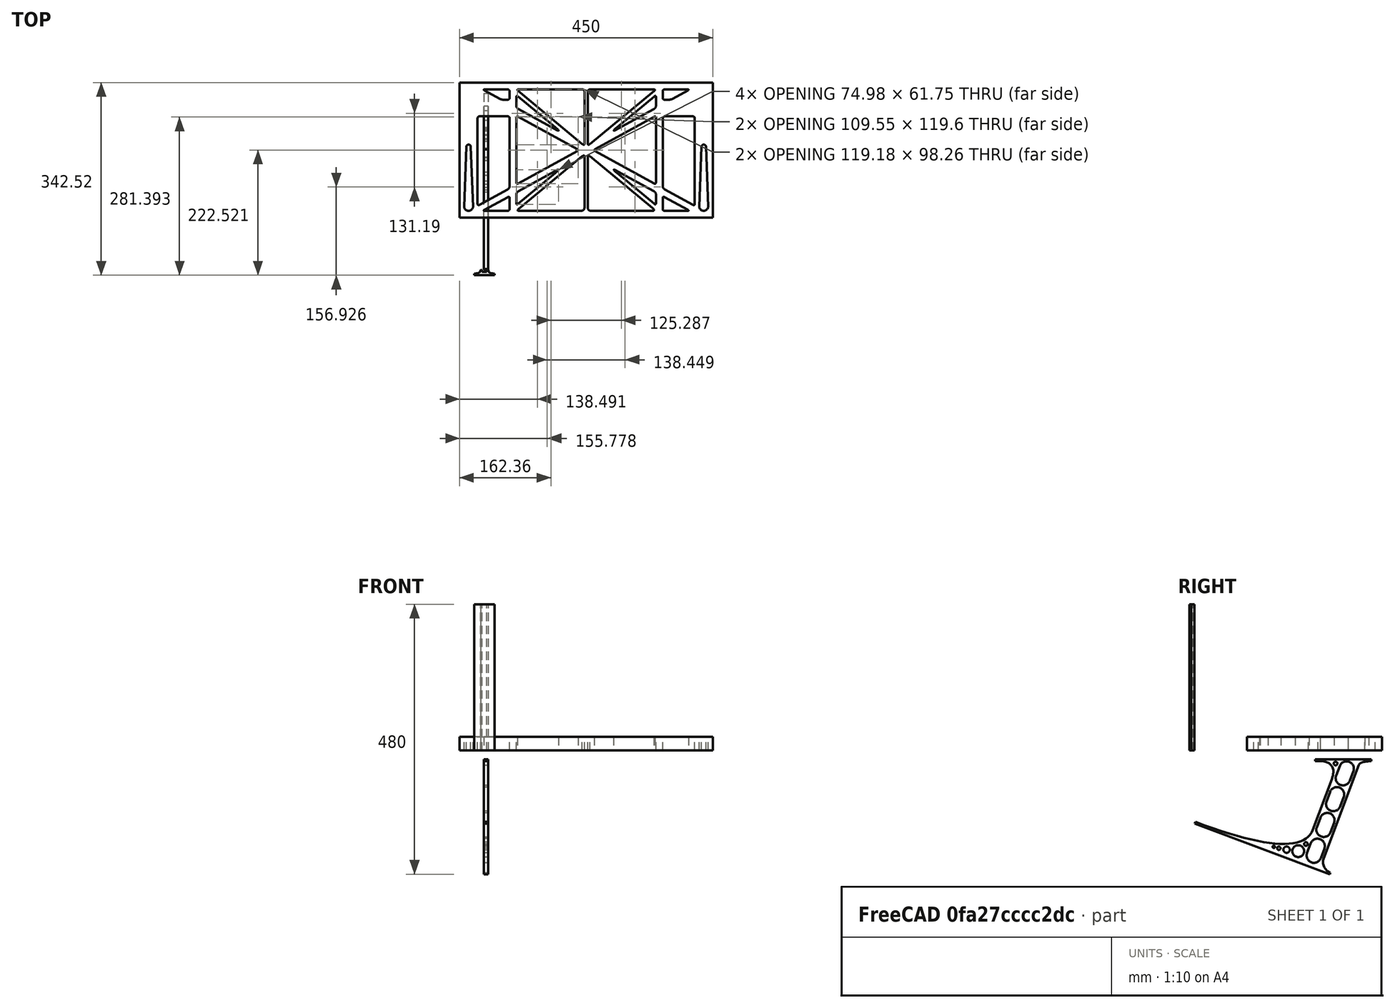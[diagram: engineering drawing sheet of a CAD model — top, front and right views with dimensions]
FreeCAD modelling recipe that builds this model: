
FCSTD DOCUMENT  (FreeCAD 0.19R0.19.2)
Label: laptopStand167FCStd
License: All rights reserved
LicenseURL: http://en.wikipedia.org/wiki/All_rights_reserved
objects: Sketcher::SketchObject×4, Part::Extrusion×3
note: 7 computed .brp shape members not serialized (recipe doc carries the construction recipe); baked Part::Feature solids carry a one-line shape summary decoded from their .brp

FEATURE [Sketcher::SketchObject] Sketch
  FullyConstrained = false
  sketch-geometry (349):
    g0: LineSegment StartX=-10.9272 StartY=-82.7794 StartZ=0 EndX=46.0728 EndY=-51.4823 EndZ=0
    g1: LineSegment StartX=-10.9272 StartY=76.4095 StartZ=0 EndX=-10.9272 EndY=-82.7794 EndZ=0
    g2: LineSegment StartX=46.0728 StartY=76.4095 StartZ=0 EndX=46.0728 EndY=-51.4823 EndZ=0
    g3: LineSegment StartX=-42.9272 StartY=136.221 StartZ=0 EndX=-42.9272 EndY=-103.779 EndZ=0
    g4: LineSegment StartX=407.073 StartY=136.221 StartZ=0 EndX=407.073 EndY=-103.779 EndZ=0
    g5: ArcOfCircle CenterX=-26.9272 CenterY=-83.7794 CenterZ=0 NormalX=0 NormalY=0 NormalZ=1 AngleXU=0 Radius=8 StartAngle=3.14159 EndAngle=6.28319
    g6: ArcOfCircle CenterX=391.073 CenterY=22.1087 CenterZ=0 NormalX=0 NormalY=0 NormalZ=1 AngleXU=0 Radius=8 StartAngle=-4.4e-15 EndAngle=3.14159
    g7: LineSegment StartX=399.073 StartY=22.1087 StartZ=0 EndX=399.073 EndY=-83.7794 EndZ=0
    g8: LineSegment StartX=383.073 StartY=22.1087 StartZ=0 EndX=383.073 EndY=-83.7794 EndZ=0
    g9: ArcOfCircle CenterX=391.073 CenterY=-83.7794 CenterZ=0 NormalX=0 NormalY=0 NormalZ=1 AngleXU=0 Radius=8 StartAngle=3.14159 EndAngle=6.28319
    g10: Circle CenterX=175.022 CenterY=27.0628 CenterZ=0 NormalX=0 NormalY=0 NormalZ=1 AngleXU=0 Radius=1
    g11: Circle CenterX=179.022 CenterY=24.8665 CenterZ=0 NormalX=0 NormalY=0 NormalZ=1 AngleXU=0 Radius=1
    g12: Circle CenterX=179.022 CenterY=27.0628 CenterZ=0 NormalX=0 NormalY=0 NormalZ=1 AngleXU=0 Radius=1
    g13: BSplineCurve PolesCount=3 KnotsCount=2 Degree=2 IsPeriodic=0
    g14: GeomPoint X=175.022 Y=27.0628 Z=0
    g15: GeomPoint X=179.022 Y=27.0628 Z=0
    g16: Circle CenterX=189.124 CenterY=27.0628 CenterZ=0 NormalX=0 NormalY=0 NormalZ=1 AngleXU=0 Radius=1
    g17: Circle CenterX=185.124 CenterY=24.8665 CenterZ=0 NormalX=0 NormalY=0 NormalZ=1 AngleXU=0 Radius=1
    g18: Circle CenterX=185.124 CenterY=27.0628 CenterZ=0 NormalX=0 NormalY=0 NormalZ=1 AngleXU=0 Radius=1
    g19: BSplineCurve PolesCount=3 KnotsCount=2 Degree=2 IsPeriodic=0
    g20: GeomPoint X=189.124 Y=27.0628 Z=0
    g21: GeomPoint X=185.124 Y=27.0628 Z=0
    g22: Circle CenterX=175.022 CenterY=5.37834 CenterZ=0 NormalX=0 NormalY=0 NormalZ=1 AngleXU=0 Radius=1
    g23: Circle CenterX=179.022 CenterY=7.57463 CenterZ=0 NormalX=0 NormalY=0 NormalZ=1 AngleXU=0 Radius=1
    g24: Circle CenterX=179.022 CenterY=5.34704 CenterZ=0 NormalX=0 NormalY=0 NormalZ=1 AngleXU=0 Radius=1
    g25: BSplineCurve PolesCount=3 KnotsCount=2 Degree=2 IsPeriodic=0
    g26: GeomPoint X=175.022 Y=5.37834 Z=0
    g27: GeomPoint X=179.022 Y=5.34704 Z=0
    g28: Circle CenterX=189.124 CenterY=5.37834 CenterZ=0 NormalX=0 NormalY=0 NormalZ=1 AngleXU=0 Radius=1
    g29: Circle CenterX=185.124 CenterY=7.57463 CenterZ=0 NormalX=0 NormalY=0 NormalZ=1 AngleXU=0 Radius=1
    g30: Circle CenterX=185.124 CenterY=5.34704 CenterZ=0 NormalX=0 NormalY=0 NormalZ=1 AngleXU=0 Radius=1
    g31: BSplineCurve PolesCount=3 KnotsCount=2 Degree=2 IsPeriodic=0
    g32: GeomPoint X=189.124 Y=5.37834 Z=0
    g33: GeomPoint X=185.124 Y=5.34704 Z=0
    g34: Circle CenterX=165.871 CenterY=18.1458 CenterZ=0 NormalX=0 NormalY=0 NormalZ=1 AngleXU=0 Radius=1
    g35: Circle CenterX=169.377 CenterY=16.2206 CenterZ=0 NormalX=0 NormalY=0 NormalZ=1 AngleXU=0 Radius=1
    g36: Circle CenterX=165.871 CenterY=14.2954 CenterZ=0 NormalX=0 NormalY=0 NormalZ=1 AngleXU=0 Radius=1
    g37: BSplineCurve PolesCount=3 KnotsCount=2 Degree=2 IsPeriodic=0
    g38: GeomPoint X=165.871 Y=18.1458 Z=0
    g39: GeomPoint X=165.871 Y=14.2954 Z=0
    g40: Circle CenterX=198.275 CenterY=18.1458 CenterZ=0 NormalX=0 NormalY=0 NormalZ=1 AngleXU=0 Radius=1
    g41: Circle CenterX=194.768 CenterY=16.2206 CenterZ=0 NormalX=0 NormalY=0 NormalZ=1 AngleXU=0 Radius=1
    g42: Circle CenterX=198.275 CenterY=14.2954 CenterZ=0 NormalX=0 NormalY=0 NormalZ=1 AngleXU=0 Radius=1
    g43: BSplineCurve PolesCount=3 KnotsCount=2 Degree=2 IsPeriodic=0
    g44: GeomPoint X=198.275 Y=18.1458 Z=0
    g45: GeomPoint X=198.275 Y=14.2954 Z=0
    g46: LineSegment StartX=407.073 StartY=-103.779 StartZ=0 EndX=-42.9272 EndY=-103.779 EndZ=0
    g47: LineSegment StartX=407.073 StartY=136.221 StartZ=0 EndX=-42.9272 EndY=136.221 EndZ=0
    g48: LineSegment StartX=46.0728 StartY=76.4095 StartZ=0 EndX=-10.9272 EndY=76.4095 EndZ=0
    g49: Circle CenterX=125.607 CenterY=54.1951 CenterZ=0 NormalX=0 NormalY=0 NormalZ=1 AngleXU=0 Radius=1
    g50: Circle CenterX=139.632 CenterY=46.4944 CenterZ=0 NormalX=0 NormalY=0 NormalZ=1 AngleXU=0 Radius=1
    g51: Circle CenterX=127.326 CenterY=56.7187 CenterZ=0 NormalX=0 NormalY=0 NormalZ=1 AngleXU=0 Radius=1
    g52: BSplineCurve PolesCount=3 KnotsCount=2 Degree=2 IsPeriodic=0
    g53: GeomPoint X=125.607 Y=54.1951 Z=0
    g54: GeomPoint X=127.326 Y=56.7187 Z=0
    g55: Circle CenterX=236.821 CenterY=56.7187 CenterZ=0 NormalX=0 NormalY=0 NormalZ=1 AngleXU=0 Radius=1
    g56: Circle CenterX=224.513 CenterY=46.4944 CenterZ=0 NormalX=0 NormalY=0 NormalZ=1 AngleXU=0 Radius=1
    g57: Circle CenterX=238.538 CenterY=54.1951 CenterZ=0 NormalX=0 NormalY=0 NormalZ=1 AngleXU=0 Radius=1
    g58: BSplineCurve PolesCount=3 KnotsCount=2 Degree=2 IsPeriodic=0
    g59: GeomPoint X=236.821 Y=56.7187 Z=0
    g60: GeomPoint X=238.538 Y=54.1951 Z=0
    g61: Circle CenterX=238.538 CenterY=-21.7539 CenterZ=0 NormalX=0 NormalY=0 NormalZ=1 AngleXU=0 Radius=1
    g62: Circle CenterX=224.513 CenterY=-14.0532 CenterZ=0 NormalX=0 NormalY=0 NormalZ=1 AngleXU=0 Radius=1
    g63: Circle CenterX=236.821 CenterY=-24.2775 CenterZ=0 NormalX=0 NormalY=0 NormalZ=1 AngleXU=0 Radius=1
    g64: BSplineCurve PolesCount=3 KnotsCount=2 Degree=2 IsPeriodic=0
    g65: GeomPoint X=238.538 Y=-21.7539 Z=0
    g66: GeomPoint X=236.821 Y=-24.2775 Z=0
    g67: Circle CenterX=125.607 CenterY=-21.7539 CenterZ=0 NormalX=0 NormalY=0 NormalZ=1 AngleXU=0 Radius=1
    g68: Circle CenterX=139.632 CenterY=-14.0532 CenterZ=0 NormalX=0 NormalY=0 NormalZ=1 AngleXU=0 Radius=1
    g69: Circle CenterX=127.325 CenterY=-24.2775 CenterZ=0 NormalX=0 NormalY=0 NormalZ=1 AngleXU=0 Radius=1
    g70: BSplineCurve PolesCount=3 KnotsCount=2 Degree=2 IsPeriodic=0
    g71: GeomPoint X=125.607 Y=-21.7539 Z=0
    g72: GeomPoint X=127.325 Y=-24.2775 Z=0
    g73: Circle CenterX=302.996 CenterY=111.695 CenterZ=0 NormalX=0 NormalY=0 NormalZ=1 AngleXU=0 Radius=1
    g74: Circle CenterX=306.073 CenterY=114.251 CenterZ=0 NormalX=0 NormalY=0 NormalZ=1 AngleXU=0 Radius=1
    g75: Circle CenterX=306.073 CenterY=110.251 CenterZ=0 NormalX=0 NormalY=0 NormalZ=1 AngleXU=0 Radius=1
    g76: BSplineCurve PolesCount=3 KnotsCount=2 Degree=2 IsPeriodic=0
    g77: GeomPoint X=302.996 Y=111.695 Z=0
    g78: GeomPoint X=306.073 Y=110.251 Z=0
    g79: Circle CenterX=306.073 CenterY=95.2763 CenterZ=0 NormalX=0 NormalY=0 NormalZ=1 AngleXU=0 Radius=1
    g80: Circle CenterX=306.073 CenterY=91.2763 CenterZ=0 NormalX=0 NormalY=0 NormalZ=1 AngleXU=0 Radius=1
    g81: Circle CenterX=302.567 CenterY=89.3511 CenterZ=0 NormalX=0 NormalY=0 NormalZ=1 AngleXU=0 Radius=1
    g82: BSplineCurve PolesCount=3 KnotsCount=2 Degree=2 IsPeriodic=0
    g83: GeomPoint X=306.073 Y=95.2763 Z=0
    g84: GeomPoint X=302.567 Y=89.3511 Z=0
    g85: LineSegment StartX=306.073 StartY=110.251 StartZ=0 EndX=306.073 EndY=95.2763 EndZ=0
    g86: LineSegment StartX=302.996 StartY=111.695 StartZ=0 EndX=236.821 EndY=56.7187 EndZ=0
    g87: LineSegment StartX=238.538 StartY=54.1951 StartZ=0 EndX=302.567 EndY=89.3511 EndZ=0
    g88: Circle CenterX=61.1496 CenterY=111.695 CenterZ=0 NormalX=0 NormalY=0 NormalZ=1 AngleXU=0 Radius=1
    g89: Circle CenterX=58.0728 CenterY=114.251 CenterZ=0 NormalX=0 NormalY=0 NormalZ=1 AngleXU=0 Radius=1
    g90: Circle CenterX=58.0728 CenterY=110.251 CenterZ=0 NormalX=0 NormalY=0 NormalZ=1 AngleXU=0 Radius=1
    g91: BSplineCurve PolesCount=3 KnotsCount=2 Degree=2 IsPeriodic=0
    g92: GeomPoint X=61.1496 Y=111.695 Z=0
    g93: GeomPoint X=58.0728 Y=110.251 Z=0
    g94: Circle CenterX=61.5791 CenterY=89.3511 CenterZ=0 NormalX=0 NormalY=0 NormalZ=1 AngleXU=0 Radius=1
    g95: Circle CenterX=58.0728 CenterY=91.2763 CenterZ=0 NormalX=0 NormalY=0 NormalZ=1 AngleXU=0 Radius=1
    g96: Circle CenterX=58.0728 CenterY=95.2763 CenterZ=0 NormalX=0 NormalY=0 NormalZ=1 AngleXU=0 Radius=1
    g97: BSplineCurve PolesCount=3 KnotsCount=2 Degree=2 IsPeriodic=0
    g98: GeomPoint X=61.5791 Y=89.3511 Z=0
    g99: GeomPoint X=58.0728 Y=95.2763 Z=0
    g100: LineSegment StartX=58.0728 StartY=110.251 StartZ=0 EndX=58.0728 EndY=95.2763 EndZ=0
    g101: LineSegment StartX=61.1496 StartY=111.695 StartZ=0 EndX=127.326 EndY=56.7187 EndZ=0
    g102: LineSegment StartX=125.607 StartY=54.1951 StartZ=0 EndX=61.5791 EndY=89.3511 EndZ=0
    g103: Circle CenterX=61.5791 CenterY=-56.9099 CenterZ=0 NormalX=0 NormalY=0 NormalZ=1 AngleXU=0 Radius=1
    g104: Circle CenterX=58.0728 CenterY=-58.8351 CenterZ=0 NormalX=0 NormalY=0 NormalZ=1 AngleXU=0 Radius=1
    g105: Circle CenterX=58.0728 CenterY=-62.8351 CenterZ=0 NormalX=0 NormalY=0 NormalZ=1 AngleXU=0 Radius=1
    g106: BSplineCurve PolesCount=3 KnotsCount=2 Degree=2 IsPeriodic=0
    g107: GeomPoint X=61.5791 Y=-56.9099 Z=0
    g108: GeomPoint X=58.0728 Y=-62.8351 Z=0
    g109: Circle CenterX=58.0728 CenterY=-77.8102 CenterZ=0 NormalX=0 NormalY=0 NormalZ=1 AngleXU=0 Radius=1
    g110: Circle CenterX=58.0728 CenterY=-81.8102 CenterZ=0 NormalX=0 NormalY=0 NormalZ=1 AngleXU=0 Radius=1
    g111: Circle CenterX=61.1496 CenterY=-79.2541 CenterZ=0 NormalX=0 NormalY=0 NormalZ=1 AngleXU=0 Radius=1
    g112: BSplineCurve PolesCount=3 KnotsCount=2 Degree=2 IsPeriodic=0
    g113: GeomPoint X=58.0728 Y=-77.8102 Z=0
    g114: GeomPoint X=61.1496 Y=-79.2541 Z=0
    g115: LineSegment StartX=58.0728 StartY=-62.8351 StartZ=0 EndX=58.0728 EndY=-77.8102 EndZ=0
    g116: LineSegment StartX=61.1496 StartY=-79.2541 StartZ=0 EndX=127.325 EndY=-24.2775 EndZ=0
    g117: LineSegment StartX=125.607 StartY=-21.7539 StartZ=0 EndX=61.5791 EndY=-56.9099 EndZ=0
    g118: Circle CenterX=302.567 CenterY=-56.9099 CenterZ=0 NormalX=0 NormalY=0 NormalZ=1 AngleXU=0 Radius=1
    g119: Circle CenterX=306.073 CenterY=-58.8351 CenterZ=0 NormalX=0 NormalY=0 NormalZ=1 AngleXU=0 Radius=1
    g120: Circle CenterX=306.073 CenterY=-62.8351 CenterZ=0 NormalX=0 NormalY=0 NormalZ=1 AngleXU=0 Radius=1
    g121: BSplineCurve PolesCount=3 KnotsCount=2 Degree=2 IsPeriodic=0
    g122: GeomPoint X=302.567 Y=-56.9099 Z=0
    g123: GeomPoint X=306.073 Y=-62.8351 Z=0
    g124: Circle CenterX=302.996 CenterY=-79.2541 CenterZ=0 NormalX=0 NormalY=0 NormalZ=1 AngleXU=0 Radius=1
    g125: Circle CenterX=306.073 CenterY=-81.8102 CenterZ=0 NormalX=0 NormalY=0 NormalZ=1 AngleXU=0 Radius=1
    g126: Circle CenterX=306.073 CenterY=-77.8102 CenterZ=0 NormalX=0 NormalY=0 NormalZ=1 AngleXU=0 Radius=1
    g127: BSplineCurve PolesCount=3 KnotsCount=2 Degree=2 IsPeriodic=0
    g128: GeomPoint X=302.996 Y=-79.2541 Z=0
    g129: GeomPoint X=306.073 Y=-77.8102 Z=0
    g130: LineSegment StartX=306.073 StartY=-62.8351 StartZ=0 EndX=306.073 EndY=-77.8102 EndZ=0
    g131: LineSegment StartX=302.996 StartY=-79.2541 StartZ=0 EndX=236.821 EndY=-24.2775 EndZ=0
    g132: LineSegment StartX=238.538 StartY=-21.7539 StartZ=0 EndX=302.567 EndY=-56.9099 EndZ=0
    g133: Circle CenterX=61.6457 CenterY=-88.8112 CenterZ=0 NormalX=0 NormalY=0 NormalZ=1 AngleXU=0 Radius=1
    g134: Circle CenterX=58.0728 CenterY=-91.7794 CenterZ=0 NormalX=0 NormalY=0 NormalZ=1 AngleXU=0 Radius=1
    g135: Circle CenterX=63.9135 CenterY=-91.7794 CenterZ=0 NormalX=0 NormalY=0 NormalZ=1 AngleXU=0 Radius=1
    g136: BSplineCurve PolesCount=3 KnotsCount=2 Degree=2 IsPeriodic=0
    g137: GeomPoint X=61.6457 Y=-88.8112 Z=0
    g138: GeomPoint X=63.9135 Y=-91.7794 Z=0
    g139: Circle CenterX=179.022 CenterY=-85.8163 CenterZ=0 NormalX=0 NormalY=0 NormalZ=1 AngleXU=0 Radius=1
    g140: Circle CenterX=179.022 CenterY=-91.7794 CenterZ=0 NormalX=0 NormalY=0 NormalZ=1 AngleXU=0 Radius=1
    g141: Circle CenterX=171.895 CenterY=-91.7794 CenterZ=0 NormalX=0 NormalY=0 NormalZ=1 AngleXU=0 Radius=1
    g142: BSplineCurve PolesCount=3 KnotsCount=2 Degree=2 IsPeriodic=0
    g143: GeomPoint X=179.022 Y=-85.8163 Z=0
    g144: GeomPoint X=171.895 Y=-91.7794 Z=0
    g145: Circle CenterX=185.124 CenterY=-86.2028 CenterZ=0 NormalX=0 NormalY=0 NormalZ=1 AngleXU=0 Radius=1
    g146: Circle CenterX=185.124 CenterY=-91.7794 CenterZ=0 NormalX=0 NormalY=0 NormalZ=1 AngleXU=0 Radius=1
    g147: Circle CenterX=191.747 CenterY=-91.7794 CenterZ=0 NormalX=0 NormalY=0 NormalZ=1 AngleXU=0 Radius=1
    g148: BSplineCurve PolesCount=3 KnotsCount=2 Degree=2 IsPeriodic=0
    g149: GeomPoint X=185.124 Y=-86.2028 Z=0
    g150: GeomPoint X=191.747 Y=-91.7794 Z=0
    g151: Circle CenterX=299.888 CenterY=-86.6413 CenterZ=0 NormalX=0 NormalY=0 NormalZ=1 AngleXU=0 Radius=1
    g152: Circle CenterX=306.073 CenterY=-91.7794 CenterZ=0 NormalX=0 NormalY=0 NormalZ=1 AngleXU=0 Radius=1
    g153: Circle CenterX=298.776 CenterY=-91.7794 CenterZ=0 NormalX=0 NormalY=0 NormalZ=1 AngleXU=0 Radius=1
    g154: BSplineCurve PolesCount=3 KnotsCount=2 Degree=2 IsPeriodic=0
    g155: GeomPoint X=299.888 Y=-86.6413 Z=0
    g156: GeomPoint X=298.776 Y=-91.7794 Z=0
    g157: LineSegment StartX=189.124 StartY=5.37834 StartZ=0 EndX=299.888 EndY=-86.6413 EndZ=0
    g158: LineSegment StartX=298.776 StartY=-91.7794 StartZ=0 EndX=191.747 EndY=-91.7794 EndZ=0
    g159: LineSegment StartX=185.124 StartY=-86.2028 StartZ=0 EndX=185.124 EndY=5.34704 EndZ=0
    g160: LineSegment StartX=179.022 StartY=5.34704 StartZ=0 EndX=179.022 EndY=-85.8163 EndZ=0
    g161: LineSegment StartX=171.895 StartY=-91.7794 StartZ=0 EndX=63.9135 EndY=-91.7794 EndZ=0
    g162: LineSegment StartX=61.6457 StartY=-88.8112 StartZ=0 EndX=175.022 EndY=5.37834 EndZ=0
    g163: Circle CenterX=302.073 CenterY=124.221 CenterZ=0 NormalX=0 NormalY=0 NormalZ=1 AngleXU=0 Radius=1
    g164: Circle CenterX=306.073 CenterY=124.221 CenterZ=0 NormalX=0 NormalY=0 NormalZ=1 AngleXU=0 Radius=1
    g165: Circle CenterX=302.996 CenterY=121.665 CenterZ=0 NormalX=0 NormalY=0 NormalZ=1 AngleXU=0 Radius=1
    g166: BSplineCurve PolesCount=3 KnotsCount=2 Degree=2 IsPeriodic=0
    g167: GeomPoint X=302.073 Y=124.221 Z=0
    g168: GeomPoint X=302.996 Y=121.665 Z=0
    g169: Circle CenterX=189.124 CenterY=124.221 CenterZ=0 NormalX=0 NormalY=0 NormalZ=1 AngleXU=0 Radius=1
    g170: Circle CenterX=185.124 CenterY=124.221 CenterZ=0 NormalX=0 NormalY=0 NormalZ=1 AngleXU=0 Radius=1
    g171: Circle CenterX=185.124 CenterY=120.221 CenterZ=0 NormalX=0 NormalY=0 NormalZ=1 AngleXU=0 Radius=1
    g172: BSplineCurve PolesCount=3 KnotsCount=2 Degree=2 IsPeriodic=0
    g173: GeomPoint X=189.124 Y=124.221 Z=0
    g174: GeomPoint X=185.124 Y=120.221 Z=0
    g175: Circle CenterX=175.022 CenterY=124.221 CenterZ=0 NormalX=0 NormalY=0 NormalZ=1 AngleXU=0 Radius=1
    g176: Circle CenterX=179.022 CenterY=124.221 CenterZ=0 NormalX=0 NormalY=0 NormalZ=1 AngleXU=0 Radius=1
    g177: Circle CenterX=179.022 CenterY=120.221 CenterZ=0 NormalX=0 NormalY=0 NormalZ=1 AngleXU=0 Radius=1
    g178: BSplineCurve PolesCount=3 KnotsCount=2 Degree=2 IsPeriodic=0
    g179: GeomPoint X=175.022 Y=124.221 Z=0
    g180: GeomPoint X=179.022 Y=120.221 Z=0
    g181: Circle CenterX=62.0728 CenterY=124.221 CenterZ=0 NormalX=0 NormalY=0 NormalZ=1 AngleXU=0 Radius=1
    g182: Circle CenterX=58.0728 CenterY=124.221 CenterZ=0 NormalX=0 NormalY=0 NormalZ=1 AngleXU=0 Radius=1
    g183: Circle CenterX=61.1496 CenterY=121.665 CenterZ=0 NormalX=0 NormalY=0 NormalZ=1 AngleXU=0 Radius=1
    g184: BSplineCurve PolesCount=3 KnotsCount=2 Degree=2 IsPeriodic=0
    g185: GeomPoint X=62.0728 Y=124.221 Z=0
    g186: GeomPoint X=61.1496 Y=121.665 Z=0
    g187: LineSegment StartX=62.0728 StartY=124.221 StartZ=0 EndX=175.022 EndY=124.221 EndZ=0
    g188: LineSegment StartX=179.022 StartY=120.221 StartZ=0 EndX=179.022 EndY=27.0628 EndZ=0
    g189: LineSegment StartX=185.124 StartY=27.0628 StartZ=0 EndX=185.124 EndY=120.221 EndZ=0
    g190: LineSegment StartX=189.124 StartY=124.221 StartZ=0 EndX=302.073 EndY=124.221 EndZ=0
    g191: LineSegment StartX=302.996 StartY=121.665 StartZ=0 EndX=189.124 EndY=27.0628 EndZ=0
    g192: LineSegment StartX=175.022 StartY=27.0628 StartZ=0 EndX=61.1496 EndY=121.665 EndZ=0
    g193: Circle CenterX=61.5791 CenterY=75.4095 CenterZ=0 NormalX=0 NormalY=0 NormalZ=1 AngleXU=0 Radius=1
    g194: Circle CenterX=58.0728 CenterY=77.3346 CenterZ=0 NormalX=0 NormalY=0 NormalZ=1 AngleXU=0 Radius=1
    g195: Circle CenterX=58.0728 CenterY=73.3346 CenterZ=0 NormalX=0 NormalY=0 NormalZ=1 AngleXU=0 Radius=1
    g196: BSplineCurve PolesCount=3 KnotsCount=2 Degree=2 IsPeriodic=0
    g197: GeomPoint X=61.5791 Y=75.4095 Z=0
    g198: GeomPoint X=58.0728 Y=73.3346 Z=0
    g199: Circle CenterX=58.0728 CenterY=-40.8935 CenterZ=0 NormalX=0 NormalY=0 NormalZ=1 AngleXU=0 Radius=1
    g200: Circle CenterX=58.0728 CenterY=-44.8935 CenterZ=0 NormalX=0 NormalY=0 NormalZ=1 AngleXU=0 Radius=1
    g201: Circle CenterX=61.5791 CenterY=-42.9683 CenterZ=0 NormalX=0 NormalY=0 NormalZ=1 AngleXU=0 Radius=1
    g202: BSplineCurve PolesCount=3 KnotsCount=2 Degree=2 IsPeriodic=0
    g203: GeomPoint X=58.0728 Y=-40.8935 Z=0
    g204: GeomPoint X=61.5791 Y=-42.9683 Z=0
    g205: LineSegment StartX=61.5791 StartY=-42.9683 StartZ=0 EndX=165.871 EndY=14.2954 EndZ=0
    g206: LineSegment StartX=165.871 StartY=18.1458 StartZ=0 EndX=61.5791 EndY=75.4095 EndZ=0
    g207: LineSegment StartX=58.0728 StartY=73.3346 StartZ=0 EndX=58.0728 EndY=-40.8935 EndZ=0
    g208: Circle CenterX=302.567 CenterY=-42.9683 CenterZ=0 NormalX=0 NormalY=0 NormalZ=1 AngleXU=0 Radius=1
    g209: Circle CenterX=306.073 CenterY=-44.8935 CenterZ=0 NormalX=0 NormalY=0 NormalZ=1 AngleXU=0 Radius=1
    g210: Circle CenterX=306.073 CenterY=-40.8935 CenterZ=0 NormalX=0 NormalY=0 NormalZ=1 AngleXU=0 Radius=1
    g211: BSplineCurve PolesCount=3 KnotsCount=2 Degree=2 IsPeriodic=0
    g212: GeomPoint X=302.567 Y=-42.9683 Z=0
    g213: GeomPoint X=306.073 Y=-40.8935 Z=0
    g214: Circle CenterX=306.073 CenterY=73.3346 CenterZ=0 NormalX=0 NormalY=0 NormalZ=1 AngleXU=0 Radius=1
    g215: Circle CenterX=306.073 CenterY=77.3346 CenterZ=0 NormalX=0 NormalY=0 NormalZ=1 AngleXU=0 Radius=1
    g216: Circle CenterX=302.567 CenterY=75.4095 CenterZ=0 NormalX=0 NormalY=0 NormalZ=1 AngleXU=0 Radius=1
    g217: BSplineCurve PolesCount=3 KnotsCount=2 Degree=2 IsPeriodic=0
    g218: GeomPoint X=306.073 Y=73.3346 Z=0
    g219: GeomPoint X=302.567 Y=75.4095 Z=0
    g220: LineSegment StartX=302.567 StartY=-42.9683 StartZ=0 EndX=198.275 EndY=14.2954 EndZ=0
    g221: LineSegment StartX=198.275 StartY=18.1458 StartZ=0 EndX=302.567 EndY=75.4095 EndZ=0
    g222: LineSegment StartX=306.073 StartY=73.3346 StartZ=0 EndX=306.073 EndY=-40.8935 EndZ=0
    g223: LineSegment StartX=322.073 StartY=105.865 StartZ=0 EndX=328.643 EndY=105.865 EndZ=0
    g224: LineSegment StartX=318.073 StartY=120.221 StartZ=0 EndX=318.073 EndY=109.865 EndZ=0
    g225: LineSegment StartX=336.157 StartY=107.779 StartZ=0 EndX=362.567 EndY=122.294 EndZ=0
    g226: Circle CenterX=362.073 CenterY=124.221 CenterZ=0 NormalX=0 NormalY=0 NormalZ=1 AngleXU=0 Radius=1
    g227: Circle CenterX=366.073 CenterY=124.221 CenterZ=0 NormalX=0 NormalY=0 NormalZ=1 AngleXU=0 Radius=1
    g228: Circle CenterX=362.567 CenterY=122.294 CenterZ=0 NormalX=0 NormalY=0 NormalZ=1 AngleXU=0 Radius=1
    g229: BSplineCurve PolesCount=3 KnotsCount=2 Degree=2 IsPeriodic=0
    g230: GeomPoint X=362.073 Y=124.221 Z=0
    g231: GeomPoint X=362.567 Y=122.294 Z=0
    g232: Circle CenterX=322.073 CenterY=124.221 CenterZ=0 NormalX=0 NormalY=0 NormalZ=1 AngleXU=0 Radius=1
    g233: Circle CenterX=318.073 CenterY=124.221 CenterZ=0 NormalX=0 NormalY=0 NormalZ=1 AngleXU=0 Radius=1
    g234: Circle CenterX=318.073 CenterY=120.221 CenterZ=0 NormalX=0 NormalY=0 NormalZ=1 AngleXU=0 Radius=1
    g235: BSplineCurve PolesCount=3 KnotsCount=2 Degree=2 IsPeriodic=0
    g236: GeomPoint X=322.073 Y=124.221 Z=0
    g237: GeomPoint X=318.073 Y=120.221 Z=0
    g238: Circle CenterX=322.073 CenterY=105.865 CenterZ=0 NormalX=0 NormalY=0 NormalZ=1 AngleXU=0 Radius=1
    g239: Circle CenterX=318.073 CenterY=105.865 CenterZ=0 NormalX=0 NormalY=0 NormalZ=1 AngleXU=0 Radius=1
    g240: Circle CenterX=318.073 CenterY=109.865 CenterZ=0 NormalX=0 NormalY=0 NormalZ=1 AngleXU=0 Radius=1
    g241: BSplineCurve PolesCount=3 KnotsCount=2 Degree=2 IsPeriodic=0
    g242: GeomPoint X=322.073 Y=105.865 Z=0
    g243: GeomPoint X=318.073 Y=109.865 Z=0
    g244: Circle CenterX=336.157 CenterY=107.779 CenterZ=0 NormalX=0 NormalY=0 NormalZ=1 AngleXU=0 Radius=1
    g245: Circle CenterX=332.651 CenterY=105.853 CenterZ=0 NormalX=0 NormalY=0 NormalZ=1 AngleXU=0 Radius=1
    g246: Circle CenterX=328.643 CenterY=105.865 CenterZ=0 NormalX=0 NormalY=0 NormalZ=1 AngleXU=0 Radius=1
    g247: BSplineCurve PolesCount=3 KnotsCount=2 Degree=2 IsPeriodic=0
    g248: GeomPoint X=336.157 Y=107.779 Z=0
    g249: GeomPoint X=328.643 Y=105.865 Z=0
    g250: LineSegment StartX=322.073 StartY=124.221 StartZ=0 EndX=362.073 EndY=124.221 EndZ=0
    g251: Circle CenterX=371.567 CenterY=-80.8644 CenterZ=0 NormalX=0 NormalY=0 NormalZ=1 AngleXU=0 Radius=1
    g252: Circle CenterX=375.073 CenterY=-82.7896 CenterZ=0 NormalX=0 NormalY=0 NormalZ=1 AngleXU=0 Radius=1
    g253: Circle CenterX=375.073 CenterY=-78.7896 CenterZ=0 NormalX=0 NormalY=0 NormalZ=1 AngleXU=0 Radius=1
    g254: BSplineCurve PolesCount=3 KnotsCount=2 Degree=2 IsPeriodic=0
    g255: GeomPoint X=371.567 Y=-80.8644 Z=0
    g256: GeomPoint X=375.073 Y=-78.7896 Z=0
    g257: Circle CenterX=321.579 CenterY=-53.4075 CenterZ=0 NormalX=0 NormalY=0 NormalZ=1 AngleXU=0 Radius=1
    g258: Circle CenterX=318.073 CenterY=-51.4823 CenterZ=0 NormalX=0 NormalY=0 NormalZ=1 AngleXU=0 Radius=1
    g259: Circle CenterX=318.073 CenterY=-47.4805 CenterZ=0 NormalX=0 NormalY=0 NormalZ=1 AngleXU=0 Radius=1
    g260: BSplineCurve PolesCount=3 KnotsCount=2 Degree=2 IsPeriodic=0
    g261: GeomPoint X=321.579 Y=-53.4075 Z=0
    g262: GeomPoint X=318.073 Y=-47.4805 Z=0
    g263: LineSegment StartX=371.567 StartY=-80.8644 StartZ=0 EndX=321.579 EndY=-53.4075 EndZ=0
    g264: Circle CenterX=321.579 CenterY=-67.3492 CenterZ=0 NormalX=0 NormalY=0 NormalZ=1 AngleXU=0 Radius=1
    g265: Circle CenterX=318.073 CenterY=-65.424 CenterZ=0 NormalX=0 NormalY=0 NormalZ=1 AngleXU=0 Radius=1
    g266: Circle CenterX=318.073 CenterY=-69.424 CenterZ=0 NormalX=0 NormalY=0 NormalZ=1 AngleXU=0 Radius=1
    g267: BSplineCurve PolesCount=3 KnotsCount=2 Degree=2 IsPeriodic=0
    g268: GeomPoint X=321.579 Y=-67.3492 Z=0
    g269: GeomPoint X=318.073 Y=-69.424 Z=0
    g270: Circle CenterX=362.567 CenterY=-89.8542 CenterZ=0 NormalX=0 NormalY=0 NormalZ=1 AngleXU=0 Radius=1
    g271: Circle CenterX=366.073 CenterY=-91.7794 CenterZ=0 NormalX=0 NormalY=0 NormalZ=1 AngleXU=0 Radius=1
    g272: Circle CenterX=362.073 CenterY=-91.7794 CenterZ=0 NormalX=0 NormalY=0 NormalZ=1 AngleXU=0 Radius=1
    g273: BSplineCurve PolesCount=3 KnotsCount=2 Degree=2 IsPeriodic=0
    g274: GeomPoint X=362.567 Y=-89.8542 Z=0
    g275: GeomPoint X=362.073 Y=-91.7794 Z=0
    g276: Circle CenterX=322.073 CenterY=-91.7794 CenterZ=0 NormalX=0 NormalY=0 NormalZ=1 AngleXU=0 Radius=1
    g277: Circle CenterX=318.073 CenterY=-91.7794 CenterZ=0 NormalX=0 NormalY=0 NormalZ=1 AngleXU=0 Radius=1
    g278: Circle CenterX=318.073 CenterY=-87.7794 CenterZ=0 NormalX=0 NormalY=0 NormalZ=1 AngleXU=0 Radius=1
    g279: BSplineCurve PolesCount=3 KnotsCount=2 Degree=2 IsPeriodic=0
    g280: GeomPoint X=322.073 Y=-91.7794 Z=0
    g281: GeomPoint X=318.073 Y=-87.7794 Z=0
    g282: LineSegment StartX=362.567 StartY=-89.8542 StartZ=0 EndX=321.579 EndY=-67.3492 EndZ=0
    g283: LineSegment StartX=318.073 StartY=-69.424 StartZ=0 EndX=318.073 EndY=-87.7794 EndZ=0
    g284: LineSegment StartX=322.073 StartY=-91.7794 StartZ=0 EndX=362.073 EndY=-91.7794 EndZ=0
    g285: Circle CenterX=2.07281 CenterY=124.221 CenterZ=0 NormalX=0 NormalY=0 NormalZ=1 AngleXU=0 Radius=1
    g286: Circle CenterX=1.57905 CenterY=122.295 CenterZ=0 NormalX=0 NormalY=0 NormalZ=1 AngleXU=0 Radius=1
    g287: BSplineCurve PolesCount=3 KnotsCount=2 Degree=2 IsPeriodic=0
    g288: GeomPoint X=2.07281 Y=124.221 Z=0
    g289: GeomPoint X=1.57905 Y=122.295 Z=0
    g290: Circle CenterX=42.0728 CenterY=124.221 CenterZ=0 NormalX=0 NormalY=0 NormalZ=1 AngleXU=0 Radius=1
    g291: Circle CenterX=46.0728 CenterY=124.221 CenterZ=0 NormalX=0 NormalY=0 NormalZ=1 AngleXU=0 Radius=1
    g292: Circle CenterX=46.0728 CenterY=120.221 CenterZ=0 NormalX=0 NormalY=0 NormalZ=1 AngleXU=0 Radius=1
    g293: BSplineCurve PolesCount=3 KnotsCount=2 Degree=2 IsPeriodic=0
    g294: GeomPoint X=42.0728 Y=124.221 Z=0
    g295: GeomPoint X=46.0728 Y=120.221 Z=0
    g296: Circle CenterX=46.0728 CenterY=109.865 CenterZ=0 NormalX=0 NormalY=0 NormalZ=1 AngleXU=0 Radius=1
    g297: Circle CenterX=46.0728 CenterY=105.865 CenterZ=0 NormalX=0 NormalY=0 NormalZ=1 AngleXU=0 Radius=1
    g298: Circle CenterX=42.0728 CenterY=105.865 CenterZ=0 NormalX=0 NormalY=0 NormalZ=1 AngleXU=0 Radius=1
    g299: BSplineCurve PolesCount=3 KnotsCount=2 Degree=2 IsPeriodic=0
    g300: GeomPoint X=46.0728 Y=109.865 Z=0
    g301: GeomPoint X=42.0728 Y=105.865 Z=0
    g302: Circle CenterX=35.5028 CenterY=105.865 CenterZ=0 NormalX=0 NormalY=0 NormalZ=1 AngleXU=0 Radius=1
    g303: Circle CenterX=31.5028 CenterY=105.865 CenterZ=0 NormalX=0 NormalY=0 NormalZ=1 AngleXU=0 Radius=1
    g304: Circle CenterX=27.9965 CenterY=107.79 CenterZ=0 NormalX=0 NormalY=0 NormalZ=1 AngleXU=0 Radius=1
    g305: BSplineCurve PolesCount=3 KnotsCount=2 Degree=2 IsPeriodic=0
    g306: GeomPoint X=35.5028 Y=105.865 Z=0
    g307: GeomPoint X=27.9965 Y=107.79 Z=0
    g308: LineSegment StartX=2.07281 StartY=124.221 StartZ=0 EndX=42.0728 EndY=124.221 EndZ=0
    g309: LineSegment StartX=46.0728 StartY=120.221 StartZ=0 EndX=46.0728 EndY=109.865 EndZ=0
    g310: LineSegment StartX=42.0728 StartY=105.865 StartZ=0 EndX=35.5028 EndY=105.865 EndZ=0
    g311: LineSegment StartX=27.9965 StartY=107.79 StartZ=0 EndX=1.57905 EndY=122.295 EndZ=0
    g312: Circle CenterX=42.5666 CenterY=-67.3492 CenterZ=0 NormalX=0 NormalY=0 NormalZ=1 AngleXU=0 Radius=1
    g313: Circle CenterX=46.0728 CenterY=-65.424 CenterZ=0 NormalX=0 NormalY=0 NormalZ=1 AngleXU=0 Radius=1
    g314: Circle CenterX=46.0728 CenterY=-69.424 CenterZ=0 NormalX=0 NormalY=0 NormalZ=1 AngleXU=0 Radius=1
    g315: BSplineCurve PolesCount=3 KnotsCount=2 Degree=2 IsPeriodic=0
    g316: GeomPoint X=42.5666 Y=-67.3492 Z=0
    g317: GeomPoint X=46.0728 Y=-69.424 Z=0
    g318: Circle CenterX=46.0728 CenterY=-87.7794 CenterZ=0 NormalX=0 NormalY=0 NormalZ=1 AngleXU=0 Radius=1
    g319: Circle CenterX=46.0728 CenterY=-91.7794 CenterZ=0 NormalX=0 NormalY=0 NormalZ=1 AngleXU=0 Radius=1
    g320: Circle CenterX=42.0728 CenterY=-91.7794 CenterZ=0 NormalX=0 NormalY=0 NormalZ=1 AngleXU=0 Radius=1
    g321: BSplineCurve PolesCount=3 KnotsCount=2 Degree=2 IsPeriodic=0
    g322: GeomPoint X=46.0728 Y=-87.7794 Z=0
    g323: GeomPoint X=42.0728 Y=-91.7794 Z=0
    g324: Circle CenterX=2.07281 CenterY=-91.7794 CenterZ=0 NormalX=0 NormalY=0 NormalZ=1 AngleXU=0 Radius=1
    g325: Circle CenterX=-1.92719 CenterY=-91.7794 CenterZ=0 NormalX=0 NormalY=0 NormalZ=1 AngleXU=0 Radius=1
    g326: Circle CenterX=1.57905 CenterY=-89.8542 CenterZ=0 NormalX=0 NormalY=0 NormalZ=1 AngleXU=0 Radius=1
    g327: BSplineCurve PolesCount=3 KnotsCount=2 Degree=2 IsPeriodic=0
    g328: GeomPoint X=2.07281 Y=-91.7794 Z=0
    g329: GeomPoint X=1.57905 Y=-89.8542 Z=0
    g330: LineSegment StartX=2.07281 StartY=-91.7794 StartZ=0 EndX=42.0728 EndY=-91.7794 EndZ=0
    g331: LineSegment StartX=46.0728 StartY=-87.7794 StartZ=0 EndX=46.0728 EndY=-69.424 EndZ=0
    g332: LineSegment StartX=42.5666 StartY=-67.3492 StartZ=0 EndX=1.57905 EndY=-89.8542 EndZ=0
    g333: Circle CenterX=322.073 CenterY=76.4095 CenterZ=0 NormalX=0 NormalY=0 NormalZ=1 AngleXU=0 Radius=4
    g334: BSplineCurve PolesCount=3 KnotsCount=2 Degree=2 IsPeriodic=0
    g335: GeomPoint X=318.073 Y=72.4095 Z=0
    g336: GeomPoint X=322.073 Y=76.4095 Z=0
    g337: Circle CenterX=375.073 CenterY=72.4095 CenterZ=0 NormalX=0 NormalY=0 NormalZ=1 AngleXU=0 Radius=1
    g338: Circle CenterX=375.073 CenterY=76.4095 CenterZ=0 NormalX=0 NormalY=0 NormalZ=1 AngleXU=0 Radius=1
    g339: Circle CenterX=371.073 CenterY=76.4095 CenterZ=0 NormalX=0 NormalY=0 NormalZ=1 AngleXU=0 Radius=1
    g340: BSplineCurve PolesCount=3 KnotsCount=2 Degree=2 IsPeriodic=0
    g341: GeomPoint X=375.073 Y=72.4095 Z=0
    g342: GeomPoint X=371.073 Y=76.4095 Z=0
    g343: LineSegment StartX=322.073 StartY=76.4095 StartZ=0 EndX=371.073 EndY=76.4095 EndZ=0
    g344: LineSegment StartX=318.073 StartY=72.4095 StartZ=0 EndX=318.073 EndY=-47.4805 EndZ=0
    g345: LineSegment StartX=375.073 StartY=72.4095 StartZ=0 EndX=375.073 EndY=-78.7896 EndZ=0
    g346: ArcOfCircle CenterX=-26.9272 CenterY=22.1087 CenterZ=0 NormalX=0 NormalY=0 NormalZ=1 AngleXU=0 Radius=4 StartAngle=5e-16 EndAngle=3.14159
    g347: LineSegment StartX=-30.9272 StartY=22.1087 StartZ=0 EndX=-34.9272 EndY=-83.7794 EndZ=0
    g348: LineSegment StartX=-18.9272 StartY=-83.7794 StartZ=0 EndX=-22.9272 EndY=22.1087 EndZ=0
  constraints (572):
    c: Coincident(g0,g2)
    c: Block(g0)
    c: Block(g1)
    c: Vertical(g3)
    c: Vertical(g4)
    c: Block(g4)
    c: Block(g3)
    c: Tangent(g6,g7) = 1.5708
    c: Tangent(g7,g9) = 1.5708
    c: Equal(g6,g9)
    c: Coincident(g8,g6)
    c: Coincident(g8,g9)
    c: Block(g7)
    c: Block(g8)
    c: Weight(g10) = 1
    c: Equal(g10,g11)
    c: Equal(g10,g12)
    c: InternalAlignment(g10,g13)
    c: InternalAlignment(g11,g13)
    c: InternalAlignment(g12,g13)
    c: InternalAlignment(g14,g13)
    c: InternalAlignment(g15,g13)
    c: Weight(g16) = 1
    c: Equal(g16,g17)
    c: Equal(g16,g18)
    c: InternalAlignment(g16,g19)
    c: InternalAlignment(g17,g19)
    c: InternalAlignment(g18,g19)
    c: InternalAlignment(g20,g19)
    c: InternalAlignment(g21,g19)
    c: Block(g19)
    c: Block(g13)
    c: Weight(g22) = 1
    c: Equal(g22,g23)
    c: Equal(g22,g24)
    c: InternalAlignment(g22,g25)
    c: InternalAlignment(g23,g25)
    c: InternalAlignment(g24,g25)
    c: InternalAlignment(g26,g25)
    c: InternalAlignment(g27,g25)
    c: Weight(g28) = 1
    c: Equal(g28,g29)
    c: Equal(g28,g30)
    c: InternalAlignment(g28,g31)
    c: InternalAlignment(g29,g31)
    c: InternalAlignment(g30,g31)
    c: InternalAlignment(g32,g31)
    c: InternalAlignment(g33,g31)
    c: Block(g31)
    c: Block(g25)
    c: Weight(g34) = 1
    c: Equal(g34,g35)
    c: Equal(g34,g36)
    c: InternalAlignment(g34,g37)
    c: InternalAlignment(g35,g37)
    c: InternalAlignment(g36,g37)
    c: InternalAlignment(g38,g37)
    c: InternalAlignment(g39,g37)
    c: Weight(g40) = 1
    c: Equal(g40,g41)
    c: Equal(g40,g42)
    c: InternalAlignment(g40,g43)
    c: InternalAlignment(g41,g43)
    c: InternalAlignment(g42,g43)
    c: InternalAlignment(g44,g43)
    c: InternalAlignment(g45,g43)
    c: Block(g37)
    c: Block(g43)
    c: Coincident(g46,g4)
    c: Coincident(g46,g3)
    c: Horizontal(g46)
    c: Distance(g46) = 450
    c: Coincident(g47,g4)
    c: Coincident(g47,g3)
    c: Horizontal(g47)
    c: Horizontal(g48)
    c: Coincident(g2,g48)
    c: Block(g48)
    c: Coincident(g1,g48)
    c: Weight(g49) = 1
    c: Equal(g49,g50)
    c: Equal(g49,g51)
    c: InternalAlignment(g49,g52)
    c: InternalAlignment(g50,g52)
    c: InternalAlignment(g51,g52)
    c: InternalAlignment(g53,g52)
    c: InternalAlignment(g54,g52)
    c: Block(g52)
    c: Weight(g55) = 1
    c: Equal(g55,g56)
    c: Equal(g55,g57)
    c: InternalAlignment(g55,g58)
    c: InternalAlignment(g56,g58)
    c: InternalAlignment(g57,g58)
    c: InternalAlignment(g59,g58)
    c: InternalAlignment(g60,g58)
    c: Block(g58)
    c: Weight(g61) = 1
    c: Equal(g61,g62)
    c: Equal(g61,g63)
    c: InternalAlignment(g61,g64)
    c: InternalAlignment(g62,g64)
    c: InternalAlignment(g63,g64)
    c: InternalAlignment(g65,g64)
    c: InternalAlignment(g66,g64)
    c: Block(g64)
    c: Weight(g67) = 1
    c: Equal(g67,g68)
    c: Equal(g67,g69)
    c: InternalAlignment(g67,g70)
    c: InternalAlignment(g68,g70)
    c: InternalAlignment(g69,g70)
    c: InternalAlignment(g71,g70)
    c: InternalAlignment(g72,g70)
    c: Block(g70)
    c: Weight(g73) = 1
    c: Equal(g73,g74)
    c: Equal(g73,g75)
    c: InternalAlignment(g73,g76)
    c: InternalAlignment(g74,g76)
    c: InternalAlignment(g75,g76)
    c: InternalAlignment(g77,g76)
    c: InternalAlignment(g78,g76)
    c: Weight(g79) = 1
    c: Equal(g79,g80)
    c: Equal(g79,g81)
    c: InternalAlignment(g79,g82)
    c: InternalAlignment(g80,g82)
    c: InternalAlignment(g81,g82)
    c: InternalAlignment(g83,g82)
    c: InternalAlignment(g84,g82)
    c: Block(g76)
    c: Block(g82)
    c: Coincident(g85,g76)
    c: Coincident(g85,g82)
    c: Vertical(g85)
    c: Coincident(g86,g76)
    c: Coincident(g86,g58)
    c: Coincident(g87,g58)
    c: Coincident(g87,g82)
    c: Weight(g88) = 1
    c: Equal(g88,g89)
    c: Equal(g88,g90)
    c: InternalAlignment(g88,g91)
    c: InternalAlignment(g89,g91)
    c: InternalAlignment(g90,g91)
    c: InternalAlignment(g92,g91)
    c: InternalAlignment(g93,g91)
    c: Weight(g94) = 1
    c: Equal(g94,g95)
    c: Equal(g94,g96)
    c: InternalAlignment(g94,g97)
    c: InternalAlignment(g95,g97)
    c: InternalAlignment(g96,g97)
    c: InternalAlignment(g98,g97)
    c: InternalAlignment(g99,g97)
    c: Block(g91)
    c: Block(g97)
    c: Coincident(g100,g91)
    c: Coincident(g100,g97)
    c: Vertical(g100)
    c: Coincident(g101,g91)
    c: Coincident(g101,g52)
    c: Coincident(g102,g52)
    c: Coincident(g102,g97)
    c: Weight(g103) = 1
    c: Equal(g103,g104)
    c: Equal(g103,g105)
    c: InternalAlignment(g103,g106)
    c: InternalAlignment(g104,g106)
    c: InternalAlignment(g105,g106)
    c: InternalAlignment(g107,g106)
    c: InternalAlignment(g108,g106)
    c: Weight(g109) = 1
    c: Equal(g109,g110)
    c: Equal(g109,g111)
    c: InternalAlignment(g109,g112)
    c: InternalAlignment(g110,g112)
    c: InternalAlignment(g111,g112)
    c: InternalAlignment(g113,g112)
    c: InternalAlignment(g114,g112)
    c: Block(g106)
    c: Block(g112)
    c: Coincident(g115,g106)
    c: Coincident(g115,g112)
    c: Vertical(g115)
    c: Coincident(g116,g112)
    c: Coincident(g116,g70)
    c: Coincident(g117,g70)
    c: Coincident(g117,g106)
    c: Weight(g118) = 1
    c: Equal(g118,g119)
    c: Equal(g118,g120)
    c: InternalAlignment(g118,g121)
    c: InternalAlignment(g119,g121)
    c: InternalAlignment(g120,g121)
    c: InternalAlignment(g122,g121)
    c: InternalAlignment(g123,g121)
    c: Weight(g124) = 1
    c: Equal(g124,g125)
    c: Equal(g124,g126)
    c: InternalAlignment(g124,g127)
    c: InternalAlignment(g125,g127)
    c: InternalAlignment(g126,g127)
    c: InternalAlignment(g128,g127)
    c: InternalAlignment(g129,g127)
    c: Block(g121)
    c: Block(g127)
    c: Coincident(g130,g121)
    c: Coincident(g130,g127)
    c: Vertical(g130)
    c: Coincident(g131,g127)
    c: Coincident(g131,g64)
    c: Coincident(g132,g64)
    c: Coincident(g132,g121)
    c: Weight(g133) = 1
    c: Equal(g133,g134)
    c: Equal(g133,g135)
    c: InternalAlignment(g133,g136)
    c: InternalAlignment(g134,g136)
    c: InternalAlignment(g135,g136)
    c: InternalAlignment(g137,g136)
    c: InternalAlignment(g138,g136)
    c: Weight(g139) = 1
    c: Equal(g139,g140)
    c: Equal(g139,g141)
    c: InternalAlignment(g139,g142)
    c: InternalAlignment(g140,g142)
    c: InternalAlignment(g141,g142)
    c: InternalAlignment(g143,g142)
    c: InternalAlignment(g144,g142)
    c: Weight(g145) = 1
    c: Equal(g145,g146)
    c: Equal(g145,g147)
    c: InternalAlignment(g145,g148)
    c: InternalAlignment(g146,g148)
    c: InternalAlignment(g147,g148)
    c: InternalAlignment(g149,g148)
    c: InternalAlignment(g150,g148)
    c: Weight(g151) = 1
    c: Equal(g151,g152)
    c: Equal(g151,g153)
    c: InternalAlignment(g151,g154)
    c: InternalAlignment(g152,g154)
    c: InternalAlignment(g153,g154)
    c: InternalAlignment(g155,g154)
    c: InternalAlignment(g156,g154)
    c: Block(g154)
    c: Block(g148)
    c: Block(g142)
    c: Block(g136)
    c: Coincident(g157,g31)
    c: Coincident(g157,g154)
    c: Coincident(g158,g154)
    c: Coincident(g158,g148)
    c: Horizontal(g158)
    c: Coincident(g159,g148)
    c: Coincident(g159,g31)
    c: Vertical(g159)
    c: Coincident(g160,g25)
    c: Coincident(g160,g142)
    c: Vertical(g160)
    c: Coincident(g161,g142)
    c: Coincident(g161,g136)
    c: Horizontal(g161)
    c: Coincident(g162,g136)
    c: Coincident(g162,g25)
    c: Weight(g163) = 1
    c: Equal(g163,g164)
    c: Equal(g163,g165)
    c: InternalAlignment(g163,g166)
    c: InternalAlignment(g164,g166)
    c: InternalAlignment(g165,g166)
    c: InternalAlignment(g167,g166)
    c: InternalAlignment(g168,g166)
    c: Weight(g169) = 1
    c: Equal(g169,g170)
    c: Equal(g169,g171)
    c: InternalAlignment(g169,g172)
    c: InternalAlignment(g170,g172)
    c: InternalAlignment(g171,g172)
    c: InternalAlignment(g173,g172)
    c: InternalAlignment(g174,g172)
    c: Weight(g175) = 1
    c: Equal(g175,g176)
    c: Equal(g175,g177)
    c: InternalAlignment(g175,g178)
    c: InternalAlignment(g176,g178)
    c: InternalAlignment(g177,g178)
    c: InternalAlignment(g179,g178)
    c: InternalAlignment(g180,g178)
    c: Weight(g181) = 1
    c: Equal(g181,g182)
    c: Equal(g181,g183)
    c: InternalAlignment(g181,g184)
    c: InternalAlignment(g182,g184)
    c: InternalAlignment(g183,g184)
    c: InternalAlignment(g185,g184)
    c: InternalAlignment(g186,g184)
    c: Block(g184)
    c: Block(g178)
    c: Block(g172)
    c: Block(g166)
    c: Coincident(g187,g184)
    c: Coincident(g187,g178)
    c: Horizontal(g187)
    c: Coincident(g188,g178)
    c: Coincident(g188,g13)
    c: Vertical(g188)
    c: Coincident(g189,g19)
    c: Coincident(g189,g172)
    c: Vertical(g189)
    c: Coincident(g190,g172)
    c: Coincident(g190,g166)
    c: Horizontal(g190)
    c: Coincident(g191,g166)
    c: Coincident(g191,g19)
    c: Coincident(g192,g13)
    c: Weight(g193) = 1
    c: Equal(g193,g194)
    c: Equal(g193,g195)
    c: InternalAlignment(g193,g196)
    c: InternalAlignment(g194,g196)
    c: InternalAlignment(g195,g196)
    c: InternalAlignment(g197,g196)
    c: InternalAlignment(g198,g196)
    c: Weight(g199) = 1
    c: Equal(g199,g200)
    c: Equal(g199,g201)
    c: InternalAlignment(g199,g202)
    c: InternalAlignment(g200,g202)
    c: InternalAlignment(g201,g202)
    c: InternalAlignment(g203,g202)
    c: InternalAlignment(g204,g202)
    c: Block(g202)
    c: Block(g196)
    c: Coincident(g205,g202)
    c: Coincident(g205,g37)
    c: Coincident(g206,g37)
    c: Coincident(g206,g196)
    c: Coincident(g207,g196)
    c: Coincident(g207,g202)
    c: Vertical(g207)
    c: Weight(g208) = 1
    c: Equal(g208,g209)
    c: Equal(g208,g210)
    c: InternalAlignment(g208,g211)
    c: InternalAlignment(g209,g211)
    c: InternalAlignment(g210,g211)
    c: InternalAlignment(g212,g211)
    c: InternalAlignment(g213,g211)
    c: Weight(g214) = 1
    c: Equal(g214,g215)
    c: Equal(g214,g216)
    c: InternalAlignment(g214,g217)
    c: InternalAlignment(g215,g217)
    c: InternalAlignment(g216,g217)
    c: InternalAlignment(g218,g217)
    c: InternalAlignment(g219,g217)
    c: Block(g217)
    c: Block(g211)
    c: Coincident(g220,g211)
    c: Coincident(g220,g43)
    c: Coincident(g221,g43)
    c: Coincident(g221,g217)
    c: Coincident(g222,g217)
    c: Coincident(g222,g211)
    c: Vertical(g222)
    c: Horizontal(g223)
    c: Block(g223)
    c: Vertical(g224)
    c: Block(g224)
    c: Block(g225)
    c: Weight(g226) = 1
    c: Equal(g226,g227)
    c: Equal(g226,g228)
    c: InternalAlignment(g226,g229)
    c: InternalAlignment(g227,g229)
    c: InternalAlignment(g228,g229)
    c: InternalAlignment(g230,g229)
    c: InternalAlignment(g231,g229)
    c: Weight(g232) = 1
    c: Equal(g232,g233)
    c: Equal(g232,g234)
    c: InternalAlignment(g232,g235)
    c: InternalAlignment(g233,g235)
    c: InternalAlignment(g234,g235)
    c: InternalAlignment(g236,g235)
    c: InternalAlignment(g237,g235)
    c: Weight(g238) = 1
    c: Equal(g238,g239)
    c: Equal(g238,g240)
    c: InternalAlignment(g238,g241)
    c: InternalAlignment(g239,g241)
    c: InternalAlignment(g240,g241)
    c: InternalAlignment(g242,g241)
    c: InternalAlignment(g243,g241)
    c: Weight(g244) = 1
    c: Equal(g244,g245)
    c: Equal(g244,g246)
    c: InternalAlignment(g244,g247)
    c: InternalAlignment(g245,g247)
    c: InternalAlignment(g246,g247)
    c: InternalAlignment(g248,g247)
    c: InternalAlignment(g249,g247)
    c: Block(g229)
    c: Block(g235)
    c: Block(g241)
    c: Block(g247)
    c: Coincident(g250,g235)
    c: Coincident(g250,g229)
    c: Horizontal(g250)
    c: Block(g192)
    c: Weight(g251) = 1
    c: Equal(g251,g252)
    c: Equal(g251,g253)
    c: InternalAlignment(g251,g254)
    c: InternalAlignment(g252,g254)
    c: InternalAlignment(g253,g254)
    c: InternalAlignment(g255,g254)
    c: InternalAlignment(g256,g254)
    c: Weight(g257) = 1
    c: Equal(g257,g258)
    c: Equal(g257,g259)
    c: InternalAlignment(g257,g260)
    c: InternalAlignment(g258,g260)
    c: InternalAlignment(g259,g260)
    c: InternalAlignment(g261,g260)
    c: InternalAlignment(g262,g260)
    c: Block(g254)
    c: Block(g260)
    c: Coincident(g263,g254)
    c: Coincident(g263,g260)
    c: Weight(g264) = 1
    c: Equal(g264,g265)
    c: Equal(g264,g266)
    c: InternalAlignment(g264,g267)
    c: InternalAlignment(g265,g267)
    c: InternalAlignment(g266,g267)
    c: InternalAlignment(g268,g267)
    c: InternalAlignment(g269,g267)
    c: Weight(g270) = 1
    c: Equal(g270,g271)
    c: Equal(g270,g272)
    c: InternalAlignment(g270,g273)
    c: InternalAlignment(g271,g273)
    c: InternalAlignment(g272,g273)
    c: InternalAlignment(g274,g273)
    c: InternalAlignment(g275,g273)
    c: Weight(g276) = 1
    c: Equal(g276,g277)
    c: Equal(g276,g278)
    c: InternalAlignment(g276,g279)
    c: InternalAlignment(g277,g279)
    c: InternalAlignment(g278,g279)
    c: InternalAlignment(g280,g279)
    c: InternalAlignment(g281,g279)
    c: Block(g279)
    c: Block(g273)
    c: Block(g267)
    c: Coincident(g282,g273)
    c: Coincident(g282,g267)
    c: Coincident(g283,g267)
    c: Coincident(g283,g279)
    c: Vertical(g283)
    c: Coincident(g284,g279)
    c: Coincident(g284,g273)
    c: Horizontal(g284)
    c: Weight(g285) = 1
    c: Equal(g285,g286)
    c: InternalAlignment(g285,g287)
    c: InternalAlignment(g286,g287)
    c: InternalAlignment(g288,g287)
    c: InternalAlignment(g289,g287)
    c: Weight(g290) = 1
    c: InternalAlignment(g291,g293)
    c: InternalAlignment(g292,g293)
    c: InternalAlignment(g294,g293)
    c: InternalAlignment(g295,g293)
    c: Weight(g296) = 1
    c: Equal(g296,g297)
    c: Equal(g296,g298)
    c: InternalAlignment(g296,g299)
    c: InternalAlignment(g297,g299)
    c: InternalAlignment(g298,g299)
    c: InternalAlignment(g300,g299)
    c: InternalAlignment(g301,g299)
    c: Equal(g302,g303)
    c: Equal(g302,g304)
    c: InternalAlignment(g302,g305)
    c: InternalAlignment(g303,g305)
    c: InternalAlignment(g304,g305)
    c: InternalAlignment(g306,g305)
    c: InternalAlignment(g307,g305)
    c: Block(g293)
    c: Block(g299)
    c: Block(g305)
    c: Block(g287)
    c: Coincident(g308,g287)
    c: Coincident(g308,g293)
    c: Horizontal(g308)
    c: Coincident(g309,g293)
    c: Coincident(g309,g299)
    c: Vertical(g309)
    c: Coincident(g310,g299)
    c: Coincident(g310,g305)
    c: Horizontal(g310)
    c: Coincident(g311,g305)
    c: Coincident(g311,g287)
    c: Weight(g312) = 1
    c: Equal(g312,g313)
    c: Equal(g312,g314)
    c: InternalAlignment(g312,g315)
    c: InternalAlignment(g313,g315)
    c: InternalAlignment(g314,g315)
    c: InternalAlignment(g316,g315)
    c: InternalAlignment(g317,g315)
    c: Weight(g318) = 1
    c: Equal(g318,g319)
    c: Equal(g318,g320)
    c: InternalAlignment(g318,g321)
    c: InternalAlignment(g319,g321)
    c: InternalAlignment(g320,g321)
    c: InternalAlignment(g322,g321)
    c: InternalAlignment(g323,g321)
    c: Weight(g324) = 1
    c: Equal(g324,g325)
    c: Equal(g324,g326)
    c: InternalAlignment(g324,g327)
    c: InternalAlignment(g325,g327)
    c: InternalAlignment(g326,g327)
    c: InternalAlignment(g328,g327)
    c: InternalAlignment(g329,g327)
    c: Block(g327)
    c: Block(g321)
    c: Block(g315)
    c: Coincident(g330,g327)
    c: Coincident(g330,g321)
    c: Horizontal(g330)
    c: Coincident(g331,g321)
    c: Coincident(g331,g315)
    c: Vertical(g331)
    c: Coincident(g332,g315)
    c: Coincident(g332,g327)
    c: InternalAlignment(g333,g334)
    c: InternalAlignment(g335,g334)
    c: InternalAlignment(g336,g334)
    c: Block(g334)
    c: Equal(g337,g338)
    c: Equal(g337,g339)
    c: InternalAlignment(g337,g340)
    c: InternalAlignment(g338,g340)
    c: InternalAlignment(g339,g340)
    c: InternalAlignment(g341,g340)
    c: InternalAlignment(g342,g340)
    c: Block(g340)
    c: Coincident(g343,g334)
    c: Horizontal(g343)
    c: Block(g343)
    c: Coincident(g344,g334)
    c: Coincident(g344,g260)
    c: Vertical(g344)
    c: Coincident(g345,g340)
    c: Coincident(g345,g254)
    c: Vertical(g345)
    c: Coincident(g347,g5)
    c: Coincident(g348,g5)
    c: Block(g346)
    c: Block(g5)
    c: Block(g348)
    c: Block(g347)
    c: Distance(g344) = 119.89
FEATURE [Sketcher::SketchObject] Sketch001
  FullyConstrained = true
  MapMode = 4
  Placement = pos=(0,0,0) rot=(0.57735,0.57735,0.57735;2.0944rad)
  Support = -> [Sketch]
  sketch-geometry (46):
    g0: BSplineCurve PolesCount=3 KnotsCount=2 Degree=2 IsPeriodic=0
    g1: ArcOfCircle CenterX=73.1223 CenterY=-32.291 CenterZ=0 NormalX=0 NormalY=0 NormalZ=1 AngleXU=0 Radius=13 StartAngle=5.92268 EndAngle=9.06428
    g2: ArcOfCircle CenterX=66.7816 CenterY=-49.1439 CenterZ=0 NormalX=0 NormalY=0 NormalZ=1 AngleXU=0 Radius=13 StartAngle=2.78068 EndAngle=5.92131
    g3: ArcOfCircle CenterX=55.9263 CenterY=-78.1807 CenterZ=0 NormalX=0 NormalY=0 NormalZ=1 AngleXU=0 Radius=13 StartAngle=5.92268 EndAngle=9.06428
    g4: ArcOfCircle CenterX=49.5884 CenterY=-95.0342 CenterZ=0 NormalX=0 NormalY=0 NormalZ=1 AngleXU=0 Radius=13 StartAngle=2.78068 EndAngle=5.92131
    g5: ArcOfCircle CenterX=38.7206 CenterY=-124.067 CenterZ=0 NormalX=0 NormalY=0 NormalZ=1 AngleXU=0 Radius=13 StartAngle=5.92268 EndAngle=9.06428
    g6: ArcOfCircle CenterX=32.3875 CenterY=-140.92 CenterZ=0 NormalX=0 NormalY=0 NormalZ=1 AngleXU=0 Radius=13 StartAngle=2.78068 EndAngle=5.92131
    g7: ArcOfCircle CenterX=21.4715 CenterY=-169.934 CenterZ=0 NormalX=0 NormalY=0 NormalZ=1 AngleXU=0 Radius=13 StartAngle=5.92268 EndAngle=9.06428
    g8: ArcOfCircle CenterX=15.1336 CenterY=-186.787 CenterZ=0 NormalX=0 NormalY=0 NormalZ=1 AngleXU=0 Radius=13 StartAngle=2.78068 EndAngle=5.92131
    g9-g12: Circle x4 (B-spline internal-alignment scaffolding for g13; pole/knot coordinates omitted)
    g13: BSplineCurve PolesCount=4 KnotsCount=2 Degree=3 IsPeriodic=0
    g14: GeomPoint X=28.8094 Y=-19.0875 Z=0
    g15: GeomPoint X=47.0443 Y=-50.4712 Z=0
    g16: Circle CenterX=53.5586 CenterY=-23.2695 CenterZ=0 NormalX=0 NormalY=0 NormalZ=1 AngleXU=0 Radius=3.24518
    g17: Circle CenterX=-195.441 CenterY=-127.082 CenterZ=0 NormalX=0 NormalY=0 NormalZ=1 AngleXU=0 Radius=1
    g18: Circle CenterX=-8.24091 CenterY=-197.481 CenterZ=0 NormalX=0 NormalY=0 NormalZ=1 AngleXU=0 Radius=1
    g19: Circle CenterX=12.8789 CenterY=-141.321 CenterZ=0 NormalX=0 NormalY=0 NormalZ=1 AngleXU=0 Radius=1
    g20: BSplineCurve PolesCount=3 KnotsCount=2 Degree=2 IsPeriodic=0
    g21: GeomPoint X=-195.441 Y=-127.082 Z=0
    g22: GeomPoint X=12.8789 Y=-141.321 Z=0
    g23: Circle CenterX=-12.8016 CenterY=-179.036 CenterZ=0 NormalX=0 NormalY=0 NormalZ=1 AngleXU=0 Radius=10.5072
    g24: Circle CenterX=0.933922 CenterY=-166.43 CenterZ=0 NormalX=0 NormalY=0 NormalZ=1 AngleXU=0 Radius=3.26661
    g25: Circle CenterX=-33.5518 CenterY=-176.44 CenterZ=0 NormalX=0 NormalY=0 NormalZ=1 AngleXU=0 Radius=5.64388
    g26: Circle CenterX=-47.2366 CenterY=-173.859 CenterZ=0 NormalX=0 NormalY=0 NormalZ=1 AngleXU=0 Radius=3.01653
    g27: Circle CenterX=-56.2595 CenterY=-171.456 CenterZ=0 NormalX=0 NormalY=0 NormalZ=1 AngleXU=0 Radius=2.12826
    g28: ArcOfCircle CenterX=51.2151 CenterY=-198.473 CenterZ=0 NormalX=0 NormalY=0 NormalZ=1 AngleXU=0 Radius=20 StartAngle=2.78189 EndAngle=4.35269
    g29: LineSegment StartX=32.4951 StartY=-191.433 StartZ=0 EndX=94.6578 EndY=-26.1352 EndZ=0
    g30: LineSegment StartX=43.1192 StartY=-220.001 StartZ=0 EndX=-196.497 EndY=-129.89 EndZ=0
    g31: LineSegment StartX=43.1192 StartY=-220.001 StartZ=0 EndX=44.1752 EndY=-217.193 EndZ=0
    g32: LineSegment StartX=117.223 StartY=-19.0875 StartZ=0 EndX=117.223 EndY=-16.0875 EndZ=0
    g33: LineSegment StartX=117.223 StartY=-16.0875 StartZ=0 EndX=17.2232 EndY=-16.0875 EndZ=0
    g34: LineSegment StartX=17.2232 StartY=-16.0875 StartZ=0 EndX=17.2232 EndY=-19.0875 EndZ=0
    g35: LineSegment StartX=28.8094 StartY=-19.0875 StartZ=0 EndX=17.2232 EndY=-19.0875 EndZ=0
    g36: LineSegment StartX=47.0443 StartY=-50.4712 StartZ=0 EndX=12.8789 EndY=-141.321 EndZ=0
    g37: LineSegment StartX=-195.441 StartY=-127.082 StartZ=0 EndX=-196.497 EndY=-129.89 EndZ=0
    g38: LineSegment StartX=85.2866 StartY=-36.8766 StartZ=0 EndX=78.9396 EndY=-53.7463 EndZ=0
    g39: LineSegment StartX=60.9579 StartY=-27.7053 StartZ=0 EndX=54.6191 EndY=-44.5532 EndZ=0
    g40: LineSegment StartX=68.0907 StartY=-82.7664 StartZ=0 EndX=61.7465 EndY=-99.6365 EndZ=0
    g41: LineSegment StartX=43.7619 StartY=-73.595 StartZ=0 EndX=37.426 EndY=-90.4435 EndZ=0
    g42: LineSegment StartX=50.885 StartY=-128.652 StartZ=0 EndX=44.5456 EndY=-145.522 EndZ=0
    g43: LineSegment StartX=26.5562 StartY=-119.481 StartZ=0 EndX=20.2251 EndY=-136.329 EndZ=0
    g44: LineSegment StartX=9.3071 StartY=-165.349 StartZ=0 EndX=2.97115 EndY=-182.197 EndZ=0
    g45: LineSegment StartX=33.6358 StartY=-174.52 StartZ=0 EndX=27.2917 EndY=-191.39 EndZ=0
  constraints (71):
    c: Block(g0)
    c: Block(g1)
    c: Block(g2)
    c: Block(g4)
    c: Block(g3)
    c: Block(g6)
    c: Block(g5)
    c: Block(g8)
    c: Block(g7)
    c: Weight(g9) = 1
    c: Equal(g9,g10)
    c: Equal(g9,g11)
    c: Equal(g9,g12)
    c: InternalAlignment(g9-g12 -> g13) x4
    c: InternalAlignment(g14,g13)
    c: InternalAlignment(g15,g13)
    c: Block(g16)
    c: Weight(g17) = 1
    c: Equal(g17,g18)
    c: Equal(g17,g19)
    c: InternalAlignment(g17,g20)
    c: InternalAlignment(g18,g20)
    c: InternalAlignment(g19,g20)
    c: InternalAlignment(g21,g20)
    c: InternalAlignment(g22,g20)
    c: Block(g20)
    c: Block(g23)
    c: Block(g24)
    c: Block(g25)
    c: Block(g26)
    c: Block(g27)
    c: Block(g28)
    c: Coincident(g29,g28)
    c: Coincident(g29,g0)
    c: Block(g13)
    c: Coincident(g31,g30)
    c: Coincident(g31,g28)
    c: Block(g31)
    c: Coincident(g32,g0)
    c: Vertical(g32)
    c: Coincident(g33,g32)
    c: Horizontal(g33)
    c: Coincident(g34,g33)
    c: Vertical(g34)
    c: Block(g33)
    c: Coincident(g35,g13)
    c: Coincident(g35,g34)
    c: Horizontal(g35)
    c: Coincident(g36,g13)
    c: Coincident(g36,g20)
    c: Coincident(g37,g20)
    c: Coincident(g37,g30)
    c: Block(g30)
    c: Coincident(g38,g1)
    c: Coincident(g38,g2)
    c: Coincident(g39,g1)
    c: Coincident(g39,g2)
    c: Coincident(g40,g3)
    c: Coincident(g40,g4)
    c: Coincident(g41,g3)
    c: Coincident(g41,g4)
    c: Coincident(g42,g5)
    c: Coincident(g42,g6)
    c: Coincident(g43,g5)
    c: Coincident(g43,g6)
    c: Coincident(g44,g7)
    c: Coincident(g44,g8)
    c: Coincident(g45,g7)
    c: Coincident(g45,g8)
    c: Distance(g30) = 256
    c: Distance(g33) = 100
FEATURE [Part::Extrusion] Extrude002
  Base = -> Sketch001
  Dir = (1,0,0)
  DirMode = 2
  FaceMakerClass = Part::FaceMakerBullseye
  LengthFwd = 8
  LengthRev = 0
  Solid = true
  Symmetric = false
FEATURE [Sketcher::SketchObject] Sketch002
  FullyConstrained = true
  sketch-geometry (20):
    g0: LineSegment StartX=-2.77179 StartY=-200.304 StartZ=0 EndX=5.22821 EndY=-200.304 EndZ=0
    g1: LineSegment StartX=5.22821 StartY=-200.304 StartZ=0 EndX=5.22821 EndY=-197.304 EndZ=0
    g2: LineSegment StartX=-2.77179 StartY=-200.304 StartZ=0 EndX=-2.77179 EndY=-197.304 EndZ=0
    g3: LineSegment StartX=5.22821 StartY=-197.304 StartZ=0 EndX=8.22821 EndY=-197.304 EndZ=0
    g4: LineSegment StartX=-2.77179 StartY=-197.304 StartZ=0 EndX=-5.77179 EndY=-197.304 EndZ=0
    g5: LineSegment StartX=19.2282 StartY=-203.304 StartZ=0 EndX=19.2282 EndY=-206.304 EndZ=0
    g6: LineSegment StartX=-16.7718 StartY=-203.304 StartZ=0 EndX=-16.7718 EndY=-206.304 EndZ=0
    g7: LineSegment StartX=-16.7718 StartY=-206.304 StartZ=0 EndX=19.2282 EndY=-206.304 EndZ=0
    g8: Circle CenterX=-16.7718 CenterY=-203.304 CenterZ=0 NormalX=0 NormalY=0 NormalZ=1 AngleXU=0 Radius=1
    g9: Circle CenterX=-5.77179 CenterY=-203.304 CenterZ=0 NormalX=0 NormalY=0 NormalZ=1 AngleXU=0 Radius=1
    g10: Circle CenterX=-5.77179 CenterY=-197.304 CenterZ=0 NormalX=0 NormalY=0 NormalZ=1 AngleXU=0 Radius=1
    g11: BSplineCurve PolesCount=3 KnotsCount=2 Degree=2 IsPeriodic=0
    g12: GeomPoint X=-16.7718 Y=-203.304 Z=0
    g13: GeomPoint X=-5.77179 Y=-197.304 Z=0
    g14: Circle CenterX=19.2282 CenterY=-203.304 CenterZ=0 NormalX=0 NormalY=0 NormalZ=1 AngleXU=0 Radius=1
    g15: Circle CenterX=8.22821 CenterY=-203.304 CenterZ=0 NormalX=0 NormalY=0 NormalZ=1 AngleXU=0 Radius=1
    g16: Circle CenterX=8.22821 CenterY=-197.304 CenterZ=0 NormalX=0 NormalY=0 NormalZ=1 AngleXU=0 Radius=1
    g17: BSplineCurve PolesCount=3 KnotsCount=2 Degree=2 IsPeriodic=0
    g18: GeomPoint X=19.2282 Y=-203.304 Z=0
    g19: GeomPoint X=8.22821 Y=-197.304 Z=0
  constraints (41):
    c: Horizontal(g0)
    c: Distance(g0) = 8
    c: Coincident(g1,g0)
    c: Vertical(g1)
    c: Distance(g1) = 3
    c: Coincident(g2,g0)
    c: Vertical(g2)
    c: Distance(g2) = 3
    c: Coincident(g3,g1)
    c: Horizontal(g3)
    c: Distance(g3) = 3
    c: Coincident(g4,g2)
    c: Horizontal(g4)
    c: Distance(g4) = 3
    c: Vertical(g5)
    c: Vertical(g6)
    c: Coincident(g7,g6)
    c: Coincident(g7,g5)
    c: Weight(g8) = 1
    c: Equal(g8,g9)
    c: Equal(g8,g10)
    c: Coincident(g11,g4)
    c: InternalAlignment(g8,g11)
    c: InternalAlignment(g9,g11)
    c: InternalAlignment(g10,g11)
    c: InternalAlignment(g12,g11)
    c: InternalAlignment(g13,g11)
    c: Coincident(g17,g5)
    c: Weight(g14) = 1
    c: Equal(g14,g15)
    c: Equal(g14,g16)
    c: Coincident(g17,g3)
    c: InternalAlignment(g14,g17)
    c: InternalAlignment(g15,g17)
    c: InternalAlignment(g16,g17)
    c: InternalAlignment(g18,g17)
    c: InternalAlignment(g19,g17)
    c: Block(g7)
    c: Block(g17)
    c: Block(g11)
    c: Block(g6)
FEATURE [Part::Extrusion] Extrude003
  Base = -> Sketch002
  Dir = (0,0,1)
  DirMode = 2
  FaceMakerClass = Part::FaceMakerBullseye
  LengthFwd = 260
  LengthRev = 0
  Solid = true
  Symmetric = false
FEATURE [Sketcher::SketchObject] Sketch003
  FullyConstrained = false
  sketch-geometry (401):
    g0: LineSegment StartX=-42.9272 StartY=136.221 StartZ=0 EndX=-42.9272 EndY=-103.779 EndZ=0
    g1: LineSegment StartX=407.073 StartY=136.221 StartZ=0 EndX=407.073 EndY=-103.779 EndZ=0
    g2: ArcOfCircle CenterX=-26.9272 CenterY=-83.7794 CenterZ=0 NormalX=0 NormalY=0 NormalZ=1 AngleXU=0 Radius=8 StartAngle=3.14159 EndAngle=6.28319
    g3: ArcOfCircle CenterX=391.073 CenterY=-83.7794 CenterZ=0 NormalX=0 NormalY=0 NormalZ=1 AngleXU=0 Radius=8 StartAngle=3.14159 EndAngle=6.28319
    g4: Circle CenterX=175.022 CenterY=27.0628 CenterZ=0 NormalX=0 NormalY=0 NormalZ=1 AngleXU=0 Radius=1
    g5: Circle CenterX=179.022 CenterY=24.8665 CenterZ=0 NormalX=0 NormalY=0 NormalZ=1 AngleXU=0 Radius=1
    g6: Circle CenterX=179.022 CenterY=27.0628 CenterZ=0 NormalX=0 NormalY=0 NormalZ=1 AngleXU=0 Radius=1
    g7: BSplineCurve PolesCount=3 KnotsCount=2 Degree=2 IsPeriodic=0
    g8: GeomPoint X=175.022 Y=27.0628 Z=0
    g9: GeomPoint X=179.022 Y=27.0628 Z=0
    g10: Circle CenterX=189.124 CenterY=27.0628 CenterZ=0 NormalX=0 NormalY=0 NormalZ=1 AngleXU=0 Radius=1
    g11: Circle CenterX=185.124 CenterY=24.8665 CenterZ=0 NormalX=0 NormalY=0 NormalZ=1 AngleXU=0 Radius=1
    g12: Circle CenterX=185.124 CenterY=27.0628 CenterZ=0 NormalX=0 NormalY=0 NormalZ=1 AngleXU=0 Radius=1
    g13: BSplineCurve PolesCount=3 KnotsCount=2 Degree=2 IsPeriodic=0
    g14: GeomPoint X=189.124 Y=27.0628 Z=0
    g15: GeomPoint X=185.124 Y=27.0628 Z=0
    g16: Circle CenterX=175.022 CenterY=5.37834 CenterZ=0 NormalX=0 NormalY=0 NormalZ=1 AngleXU=0 Radius=1
    g17: Circle CenterX=179.022 CenterY=7.57463 CenterZ=0 NormalX=0 NormalY=0 NormalZ=1 AngleXU=0 Radius=1
    g18: Circle CenterX=179.022 CenterY=5.34704 CenterZ=0 NormalX=0 NormalY=0 NormalZ=1 AngleXU=0 Radius=1
    g19: BSplineCurve PolesCount=3 KnotsCount=2 Degree=2 IsPeriodic=0
    g20: GeomPoint X=175.022 Y=5.37834 Z=0
    g21: GeomPoint X=179.022 Y=5.34704 Z=0
    g22: Circle CenterX=189.124 CenterY=5.37834 CenterZ=0 NormalX=0 NormalY=0 NormalZ=1 AngleXU=0 Radius=1
    g23: Circle CenterX=185.124 CenterY=7.57463 CenterZ=0 NormalX=0 NormalY=0 NormalZ=1 AngleXU=0 Radius=1
    g24: Circle CenterX=185.124 CenterY=5.34704 CenterZ=0 NormalX=0 NormalY=0 NormalZ=1 AngleXU=0 Radius=1
    g25: BSplineCurve PolesCount=3 KnotsCount=2 Degree=2 IsPeriodic=0
    g26: GeomPoint X=189.124 Y=5.37834 Z=0
    g27: GeomPoint X=185.124 Y=5.34704 Z=0
    g28: Circle CenterX=165.871 CenterY=18.1458 CenterZ=0 NormalX=0 NormalY=0 NormalZ=1 AngleXU=0 Radius=1
    g29: Circle CenterX=169.377 CenterY=16.2206 CenterZ=0 NormalX=0 NormalY=0 NormalZ=1 AngleXU=0 Radius=1
    g30: Circle CenterX=165.871 CenterY=14.2954 CenterZ=0 NormalX=0 NormalY=0 NormalZ=1 AngleXU=0 Radius=1
    g31: BSplineCurve PolesCount=3 KnotsCount=2 Degree=2 IsPeriodic=0
    g32: GeomPoint X=165.871 Y=18.1458 Z=0
    g33: GeomPoint X=165.871 Y=14.2954 Z=0
    g34: Circle CenterX=198.275 CenterY=18.1458 CenterZ=0 NormalX=0 NormalY=0 NormalZ=1 AngleXU=0 Radius=1
    g35: Circle CenterX=194.768 CenterY=16.2206 CenterZ=0 NormalX=0 NormalY=0 NormalZ=1 AngleXU=0 Radius=1
    g36: Circle CenterX=198.275 CenterY=14.2954 CenterZ=0 NormalX=0 NormalY=0 NormalZ=1 AngleXU=0 Radius=1
    g37: BSplineCurve PolesCount=3 KnotsCount=2 Degree=2 IsPeriodic=0
    g38: GeomPoint X=198.275 Y=18.1458 Z=0
    g39: GeomPoint X=198.275 Y=14.2954 Z=0
    g40: LineSegment StartX=407.073 StartY=-103.779 StartZ=0 EndX=-42.9272 EndY=-103.779 EndZ=0
    g41: Circle CenterX=125.607 CenterY=54.1951 CenterZ=0 NormalX=0 NormalY=0 NormalZ=1 AngleXU=0 Radius=1
    g42: Circle CenterX=139.632 CenterY=46.4944 CenterZ=0 NormalX=0 NormalY=0 NormalZ=1 AngleXU=0 Radius=1
    g43: Circle CenterX=127.326 CenterY=56.7187 CenterZ=0 NormalX=0 NormalY=0 NormalZ=1 AngleXU=0 Radius=1
    g44: BSplineCurve PolesCount=3 KnotsCount=2 Degree=2 IsPeriodic=0
    g45: GeomPoint X=125.607 Y=54.1951 Z=0
    g46: GeomPoint X=127.326 Y=56.7187 Z=0
    g47: Circle CenterX=236.821 CenterY=56.7187 CenterZ=0 NormalX=0 NormalY=0 NormalZ=1 AngleXU=0 Radius=1
    g48: Circle CenterX=224.513 CenterY=46.4944 CenterZ=0 NormalX=0 NormalY=0 NormalZ=1 AngleXU=0 Radius=1
    g49: Circle CenterX=238.538 CenterY=54.1951 CenterZ=0 NormalX=0 NormalY=0 NormalZ=1 AngleXU=0 Radius=1
    g50: BSplineCurve PolesCount=3 KnotsCount=2 Degree=2 IsPeriodic=0
    g51: GeomPoint X=236.821 Y=56.7187 Z=0
    g52: GeomPoint X=238.538 Y=54.1951 Z=0
    g53: Circle CenterX=238.538 CenterY=-21.7539 CenterZ=0 NormalX=0 NormalY=0 NormalZ=1 AngleXU=0 Radius=1
    g54: Circle CenterX=224.513 CenterY=-14.0532 CenterZ=0 NormalX=0 NormalY=0 NormalZ=1 AngleXU=0 Radius=1
    g55: Circle CenterX=236.821 CenterY=-24.2775 CenterZ=0 NormalX=0 NormalY=0 NormalZ=1 AngleXU=0 Radius=1
    g56: BSplineCurve PolesCount=3 KnotsCount=2 Degree=2 IsPeriodic=0
    g57: GeomPoint X=238.538 Y=-21.7539 Z=0
    g58: GeomPoint X=236.821 Y=-24.2775 Z=0
    g59: Circle CenterX=125.607 CenterY=-21.7539 CenterZ=0 NormalX=0 NormalY=0 NormalZ=1 AngleXU=0 Radius=1
    g60: Circle CenterX=139.632 CenterY=-14.0532 CenterZ=0 NormalX=0 NormalY=0 NormalZ=1 AngleXU=0 Radius=1
    g61: Circle CenterX=127.325 CenterY=-24.2775 CenterZ=0 NormalX=0 NormalY=0 NormalZ=1 AngleXU=0 Radius=1
    g62: BSplineCurve PolesCount=3 KnotsCount=2 Degree=2 IsPeriodic=0
    g63: GeomPoint X=125.607 Y=-21.7539 Z=0
    g64: GeomPoint X=127.325 Y=-24.2775 Z=0
    g65: Circle CenterX=302.996 CenterY=111.695 CenterZ=0 NormalX=0 NormalY=0 NormalZ=1 AngleXU=0 Radius=1
    g66: Circle CenterX=306.073 CenterY=114.251 CenterZ=0 NormalX=0 NormalY=0 NormalZ=1 AngleXU=0 Radius=1
    g67: Circle CenterX=306.073 CenterY=110.251 CenterZ=0 NormalX=0 NormalY=0 NormalZ=1 AngleXU=0 Radius=1
    g68: BSplineCurve PolesCount=3 KnotsCount=2 Degree=2 IsPeriodic=0
    g69: GeomPoint X=302.996 Y=111.695 Z=0
    g70: GeomPoint X=306.073 Y=110.251 Z=0
    g71: Circle CenterX=306.073 CenterY=95.2763 CenterZ=0 NormalX=0 NormalY=0 NormalZ=1 AngleXU=0 Radius=1
    g72: Circle CenterX=306.073 CenterY=91.2763 CenterZ=0 NormalX=0 NormalY=0 NormalZ=1 AngleXU=0 Radius=1
    g73: Circle CenterX=302.567 CenterY=89.3511 CenterZ=0 NormalX=0 NormalY=0 NormalZ=1 AngleXU=0 Radius=1
    g74: BSplineCurve PolesCount=3 KnotsCount=2 Degree=2 IsPeriodic=0
    g75: GeomPoint X=306.073 Y=95.2763 Z=0
    g76: GeomPoint X=302.567 Y=89.3511 Z=0
    g77: LineSegment StartX=306.073 StartY=110.251 StartZ=0 EndX=306.073 EndY=95.2763 EndZ=0
    g78: LineSegment StartX=302.996 StartY=111.695 StartZ=0 EndX=236.821 EndY=56.7187 EndZ=0
    g79: LineSegment StartX=238.538 StartY=54.1951 StartZ=0 EndX=302.567 EndY=89.3511 EndZ=0
    g80: Circle CenterX=61.1496 CenterY=111.695 CenterZ=0 NormalX=0 NormalY=0 NormalZ=1 AngleXU=0 Radius=1
    g81: Circle CenterX=58.0728 CenterY=114.251 CenterZ=0 NormalX=0 NormalY=0 NormalZ=1 AngleXU=0 Radius=1
    g82: Circle CenterX=58.0728 CenterY=110.251 CenterZ=0 NormalX=0 NormalY=0 NormalZ=1 AngleXU=0 Radius=1
    g83: BSplineCurve PolesCount=3 KnotsCount=2 Degree=2 IsPeriodic=0
    g84: GeomPoint X=61.1496 Y=111.695 Z=0
    g85: GeomPoint X=58.0728 Y=110.251 Z=0
    g86: Circle CenterX=61.5791 CenterY=89.3511 CenterZ=0 NormalX=0 NormalY=0 NormalZ=1 AngleXU=0 Radius=1
    g87: Circle CenterX=58.0728 CenterY=91.2763 CenterZ=0 NormalX=0 NormalY=0 NormalZ=1 AngleXU=0 Radius=1
    g88: Circle CenterX=58.0728 CenterY=95.2763 CenterZ=0 NormalX=0 NormalY=0 NormalZ=1 AngleXU=0 Radius=1
    g89: BSplineCurve PolesCount=3 KnotsCount=2 Degree=2 IsPeriodic=0
    g90: GeomPoint X=61.5791 Y=89.3511 Z=0
    g91: GeomPoint X=58.0728 Y=95.2763 Z=0
    g92: LineSegment StartX=58.0728 StartY=110.251 StartZ=0 EndX=58.0728 EndY=95.2763 EndZ=0
    g93: LineSegment StartX=61.1496 StartY=111.695 StartZ=0 EndX=127.326 EndY=56.7187 EndZ=0
    g94: LineSegment StartX=125.607 StartY=54.1951 StartZ=0 EndX=61.5791 EndY=89.3511 EndZ=0
    g95: Circle CenterX=61.5791 CenterY=-56.9099 CenterZ=0 NormalX=0 NormalY=0 NormalZ=1 AngleXU=0 Radius=1
    g96: Circle CenterX=58.0728 CenterY=-58.8351 CenterZ=0 NormalX=0 NormalY=0 NormalZ=1 AngleXU=0 Radius=1
    g97: Circle CenterX=58.0728 CenterY=-62.8351 CenterZ=0 NormalX=0 NormalY=0 NormalZ=1 AngleXU=0 Radius=1
    g98: BSplineCurve PolesCount=3 KnotsCount=2 Degree=2 IsPeriodic=0
    g99: GeomPoint X=61.5791 Y=-56.9099 Z=0
    g100: GeomPoint X=58.0728 Y=-62.8351 Z=0
    g101: Circle CenterX=58.0728 CenterY=-77.8102 CenterZ=0 NormalX=0 NormalY=0 NormalZ=1 AngleXU=0 Radius=1
    g102: Circle CenterX=58.0728 CenterY=-81.8102 CenterZ=0 NormalX=0 NormalY=0 NormalZ=1 AngleXU=0 Radius=1
    g103: Circle CenterX=61.1496 CenterY=-79.2541 CenterZ=0 NormalX=0 NormalY=0 NormalZ=1 AngleXU=0 Radius=1
    g104: BSplineCurve PolesCount=3 KnotsCount=2 Degree=2 IsPeriodic=0
    g105: GeomPoint X=58.0728 Y=-77.8102 Z=0
    g106: GeomPoint X=61.1496 Y=-79.2541 Z=0
    g107: LineSegment StartX=58.0728 StartY=-62.8351 StartZ=0 EndX=58.0728 EndY=-77.8102 EndZ=0
    g108: LineSegment StartX=61.1496 StartY=-79.2541 StartZ=0 EndX=127.325 EndY=-24.2775 EndZ=0
    g109: LineSegment StartX=125.607 StartY=-21.7539 StartZ=0 EndX=61.5791 EndY=-56.9099 EndZ=0
    g110: Circle CenterX=302.567 CenterY=-56.9099 CenterZ=0 NormalX=0 NormalY=0 NormalZ=1 AngleXU=0 Radius=1
    g111: Circle CenterX=306.073 CenterY=-58.8351 CenterZ=0 NormalX=0 NormalY=0 NormalZ=1 AngleXU=0 Radius=1
    g112: Circle CenterX=306.073 CenterY=-62.8351 CenterZ=0 NormalX=0 NormalY=0 NormalZ=1 AngleXU=0 Radius=1
    g113: BSplineCurve PolesCount=3 KnotsCount=2 Degree=2 IsPeriodic=0
    g114: GeomPoint X=302.567 Y=-56.9099 Z=0
    g115: GeomPoint X=306.073 Y=-62.8351 Z=0
    g116: Circle CenterX=302.996 CenterY=-79.2541 CenterZ=0 NormalX=0 NormalY=0 NormalZ=1 AngleXU=0 Radius=1
    g117: Circle CenterX=306.073 CenterY=-81.8102 CenterZ=0 NormalX=0 NormalY=0 NormalZ=1 AngleXU=0 Radius=1
    g118: Circle CenterX=306.073 CenterY=-77.8102 CenterZ=0 NormalX=0 NormalY=0 NormalZ=1 AngleXU=0 Radius=1
    g119: BSplineCurve PolesCount=3 KnotsCount=2 Degree=2 IsPeriodic=0
    g120: GeomPoint X=302.996 Y=-79.2541 Z=0
    g121: GeomPoint X=306.073 Y=-77.8102 Z=0
    g122: LineSegment StartX=306.073 StartY=-62.8351 StartZ=0 EndX=306.073 EndY=-77.8102 EndZ=0
    g123: LineSegment StartX=302.996 StartY=-79.2541 StartZ=0 EndX=236.821 EndY=-24.2775 EndZ=0
    g124: LineSegment StartX=238.538 StartY=-21.7539 StartZ=0 EndX=302.567 EndY=-56.9099 EndZ=0
    g125: Circle CenterX=61.6457 CenterY=-88.8112 CenterZ=0 NormalX=0 NormalY=0 NormalZ=1 AngleXU=0 Radius=1
    g126: Circle CenterX=58.0728 CenterY=-91.7794 CenterZ=0 NormalX=0 NormalY=0 NormalZ=1 AngleXU=0 Radius=1
    g127: Circle CenterX=63.9135 CenterY=-91.7794 CenterZ=0 NormalX=0 NormalY=0 NormalZ=1 AngleXU=0 Radius=1
    g128: BSplineCurve PolesCount=3 KnotsCount=2 Degree=2 IsPeriodic=0
    g129: GeomPoint X=61.6457 Y=-88.8112 Z=0
    g130: GeomPoint X=63.9135 Y=-91.7794 Z=0
    g131: Circle CenterX=179.022 CenterY=-85.8163 CenterZ=0 NormalX=0 NormalY=0 NormalZ=1 AngleXU=0 Radius=1
    g132: Circle CenterX=179.022 CenterY=-91.7794 CenterZ=0 NormalX=0 NormalY=0 NormalZ=1 AngleXU=0 Radius=1
    g133: Circle CenterX=171.895 CenterY=-91.7794 CenterZ=0 NormalX=0 NormalY=0 NormalZ=1 AngleXU=0 Radius=1
    g134: BSplineCurve PolesCount=3 KnotsCount=2 Degree=2 IsPeriodic=0
    g135: GeomPoint X=179.022 Y=-85.8163 Z=0
    g136: GeomPoint X=171.895 Y=-91.7794 Z=0
    g137: Circle CenterX=185.124 CenterY=-86.2028 CenterZ=0 NormalX=0 NormalY=0 NormalZ=1 AngleXU=0 Radius=1
    g138: Circle CenterX=185.124 CenterY=-91.7794 CenterZ=0 NormalX=0 NormalY=0 NormalZ=1 AngleXU=0 Radius=1
    g139: Circle CenterX=191.747 CenterY=-91.7794 CenterZ=0 NormalX=0 NormalY=0 NormalZ=1 AngleXU=0 Radius=1
    g140: BSplineCurve PolesCount=3 KnotsCount=2 Degree=2 IsPeriodic=0
    g141: GeomPoint X=185.124 Y=-86.2028 Z=0
    g142: GeomPoint X=191.747 Y=-91.7794 Z=0
    g143: Circle CenterX=299.888 CenterY=-86.6413 CenterZ=0 NormalX=0 NormalY=0 NormalZ=1 AngleXU=0 Radius=1
    g144: Circle CenterX=306.073 CenterY=-91.7794 CenterZ=0 NormalX=0 NormalY=0 NormalZ=1 AngleXU=0 Radius=1
    g145: Circle CenterX=298.776 CenterY=-91.7794 CenterZ=0 NormalX=0 NormalY=0 NormalZ=1 AngleXU=0 Radius=1
    g146: BSplineCurve PolesCount=3 KnotsCount=2 Degree=2 IsPeriodic=0
    g147: GeomPoint X=299.888 Y=-86.6413 Z=0
    g148: GeomPoint X=298.776 Y=-91.7794 Z=0
    g149: LineSegment StartX=189.124 StartY=5.37834 StartZ=0 EndX=299.888 EndY=-86.6413 EndZ=0
    g150: LineSegment StartX=298.776 StartY=-91.7794 StartZ=0 EndX=191.747 EndY=-91.7794 EndZ=0
    g151: LineSegment StartX=185.124 StartY=-86.2028 StartZ=0 EndX=185.124 EndY=5.34704 EndZ=0
    g152: LineSegment StartX=179.022 StartY=5.34704 StartZ=0 EndX=179.022 EndY=-85.8163 EndZ=0
    g153: LineSegment StartX=171.895 StartY=-91.7794 StartZ=0 EndX=63.9135 EndY=-91.7794 EndZ=0
    g154: LineSegment StartX=61.6457 StartY=-88.8112 StartZ=0 EndX=175.022 EndY=5.37834 EndZ=0
    g155: Circle CenterX=302.073 CenterY=124.221 CenterZ=0 NormalX=0 NormalY=0 NormalZ=1 AngleXU=0 Radius=1
    g156: Circle CenterX=306.073 CenterY=124.221 CenterZ=0 NormalX=0 NormalY=0 NormalZ=1 AngleXU=0 Radius=1
    g157: Circle CenterX=302.996 CenterY=121.665 CenterZ=0 NormalX=0 NormalY=0 NormalZ=1 AngleXU=0 Radius=1
    g158: BSplineCurve PolesCount=3 KnotsCount=2 Degree=2 IsPeriodic=0
    g159: GeomPoint X=302.073 Y=124.221 Z=0
    g160: GeomPoint X=302.996 Y=121.665 Z=0
    g161: Circle CenterX=189.124 CenterY=124.221 CenterZ=0 NormalX=0 NormalY=0 NormalZ=1 AngleXU=0 Radius=1
    g162: Circle CenterX=185.124 CenterY=124.221 CenterZ=0 NormalX=0 NormalY=0 NormalZ=1 AngleXU=0 Radius=1
    g163: Circle CenterX=185.124 CenterY=120.221 CenterZ=0 NormalX=0 NormalY=0 NormalZ=1 AngleXU=0 Radius=1
    g164: BSplineCurve PolesCount=3 KnotsCount=2 Degree=2 IsPeriodic=0
    g165: GeomPoint X=189.124 Y=124.221 Z=0
    g166: GeomPoint X=185.124 Y=120.221 Z=0
    g167: Circle CenterX=175.022 CenterY=124.221 CenterZ=0 NormalX=0 NormalY=0 NormalZ=1 AngleXU=0 Radius=1
    g168: Circle CenterX=179.022 CenterY=124.221 CenterZ=0 NormalX=0 NormalY=0 NormalZ=1 AngleXU=0 Radius=1
    g169: Circle CenterX=179.022 CenterY=120.221 CenterZ=0 NormalX=0 NormalY=0 NormalZ=1 AngleXU=0 Radius=1
    g170: BSplineCurve PolesCount=3 KnotsCount=2 Degree=2 IsPeriodic=0
    g171: GeomPoint X=175.022 Y=124.221 Z=0
    g172: GeomPoint X=179.022 Y=120.221 Z=0
    g173: Circle CenterX=62.0728 CenterY=124.221 CenterZ=0 NormalX=0 NormalY=0 NormalZ=1 AngleXU=0 Radius=1
    g174: Circle CenterX=58.0728 CenterY=124.221 CenterZ=0 NormalX=0 NormalY=0 NormalZ=1 AngleXU=0 Radius=1
    g175: Circle CenterX=61.1496 CenterY=121.665 CenterZ=0 NormalX=0 NormalY=0 NormalZ=1 AngleXU=0 Radius=1
    g176: BSplineCurve PolesCount=3 KnotsCount=2 Degree=2 IsPeriodic=0
    g177: GeomPoint X=62.0728 Y=124.221 Z=0
    g178: GeomPoint X=61.1496 Y=121.665 Z=0
    g179: LineSegment StartX=179.022 StartY=120.221 StartZ=0 EndX=179.022 EndY=27.0628 EndZ=0
    g180: LineSegment StartX=185.124 StartY=27.0628 StartZ=0 EndX=185.124 EndY=120.221 EndZ=0
    g181: LineSegment StartX=302.996 StartY=121.665 StartZ=0 EndX=189.124 EndY=27.0628 EndZ=0
    g182: LineSegment StartX=175.022 StartY=27.0628 StartZ=0 EndX=61.1496 EndY=121.665 EndZ=0
    g183: Circle CenterX=61.5791 CenterY=75.4095 CenterZ=0 NormalX=0 NormalY=0 NormalZ=1 AngleXU=0 Radius=1
    g184: Circle CenterX=58.0728 CenterY=77.3346 CenterZ=0 NormalX=0 NormalY=0 NormalZ=1 AngleXU=0 Radius=1
    g185: Circle CenterX=58.0728 CenterY=73.3346 CenterZ=0 NormalX=0 NormalY=0 NormalZ=1 AngleXU=0 Radius=1
    g186: BSplineCurve PolesCount=3 KnotsCount=2 Degree=2 IsPeriodic=0
    g187: GeomPoint X=61.5791 Y=75.4095 Z=0
    g188: GeomPoint X=58.0728 Y=73.3346 Z=0
    g189: Circle CenterX=58.0728 CenterY=-40.8935 CenterZ=0 NormalX=0 NormalY=0 NormalZ=1 AngleXU=0 Radius=1
    g190: Circle CenterX=58.0728 CenterY=-44.8935 CenterZ=0 NormalX=0 NormalY=0 NormalZ=1 AngleXU=0 Radius=1
    g191: Circle CenterX=61.5791 CenterY=-42.9683 CenterZ=0 NormalX=0 NormalY=0 NormalZ=1 AngleXU=0 Radius=1
    g192: BSplineCurve PolesCount=3 KnotsCount=2 Degree=2 IsPeriodic=0
    g193: GeomPoint X=58.0728 Y=-40.8935 Z=0
    g194: GeomPoint X=61.5791 Y=-42.9683 Z=0
    g195: LineSegment StartX=61.5791 StartY=-42.9683 StartZ=0 EndX=165.871 EndY=14.2954 EndZ=0
    g196: LineSegment StartX=165.871 StartY=18.1458 StartZ=0 EndX=61.5791 EndY=75.4095 EndZ=0
    g197: LineSegment StartX=58.0728 StartY=73.3346 StartZ=0 EndX=58.0728 EndY=-40.8935 EndZ=0
    g198: Circle CenterX=302.567 CenterY=-42.9683 CenterZ=0 NormalX=0 NormalY=0 NormalZ=1 AngleXU=0 Radius=1
    g199: Circle CenterX=306.073 CenterY=-44.8935 CenterZ=0 NormalX=0 NormalY=0 NormalZ=1 AngleXU=0 Radius=1
    g200: Circle CenterX=306.073 CenterY=-40.8935 CenterZ=0 NormalX=0 NormalY=0 NormalZ=1 AngleXU=0 Radius=1
    g201: BSplineCurve PolesCount=3 KnotsCount=2 Degree=2 IsPeriodic=0
    g202: GeomPoint X=302.567 Y=-42.9683 Z=0
    g203: GeomPoint X=306.073 Y=-40.8935 Z=0
    g204: Circle CenterX=306.073 CenterY=73.3346 CenterZ=0 NormalX=0 NormalY=0 NormalZ=1 AngleXU=0 Radius=1
    g205: Circle CenterX=306.073 CenterY=77.3346 CenterZ=0 NormalX=0 NormalY=0 NormalZ=1 AngleXU=0 Radius=1
    g206: Circle CenterX=302.567 CenterY=75.4095 CenterZ=0 NormalX=0 NormalY=0 NormalZ=1 AngleXU=0 Radius=1
    g207: BSplineCurve PolesCount=3 KnotsCount=2 Degree=2 IsPeriodic=0
    g208: GeomPoint X=306.073 Y=73.3346 Z=0
    g209: GeomPoint X=302.567 Y=75.4095 Z=0
    g210: LineSegment StartX=302.567 StartY=-42.9683 StartZ=0 EndX=198.275 EndY=14.2954 EndZ=0
    g211: LineSegment StartX=198.275 StartY=18.1458 StartZ=0 EndX=302.567 EndY=75.4095 EndZ=0
    g212: LineSegment StartX=306.073 StartY=73.3346 StartZ=0 EndX=306.073 EndY=-40.8935 EndZ=0
    g213: LineSegment StartX=322.073 StartY=105.865 StartZ=0 EndX=328.643 EndY=105.865 EndZ=0
    g214: LineSegment StartX=318.073 StartY=120.221 StartZ=0 EndX=318.073 EndY=109.865 EndZ=0
    g215: LineSegment StartX=336.157 StartY=107.779 StartZ=0 EndX=362.567 EndY=122.294 EndZ=0
    g216: Circle CenterX=362.073 CenterY=124.221 CenterZ=0 NormalX=0 NormalY=0 NormalZ=1 AngleXU=0 Radius=1
    g217: Circle CenterX=366.073 CenterY=124.221 CenterZ=0 NormalX=0 NormalY=0 NormalZ=1 AngleXU=0 Radius=1
    g218: Circle CenterX=362.567 CenterY=122.294 CenterZ=0 NormalX=0 NormalY=0 NormalZ=1 AngleXU=0 Radius=1
    g219: BSplineCurve PolesCount=3 KnotsCount=2 Degree=2 IsPeriodic=0
    g220: GeomPoint X=362.073 Y=124.221 Z=0
    g221: GeomPoint X=362.567 Y=122.294 Z=0
    g222: Circle CenterX=322.073 CenterY=124.221 CenterZ=0 NormalX=0 NormalY=0 NormalZ=1 AngleXU=0 Radius=1
    g223: Circle CenterX=318.073 CenterY=124.221 CenterZ=0 NormalX=0 NormalY=0 NormalZ=1 AngleXU=0 Radius=1
    g224: Circle CenterX=318.073 CenterY=120.221 CenterZ=0 NormalX=0 NormalY=0 NormalZ=1 AngleXU=0 Radius=1
    g225: BSplineCurve PolesCount=3 KnotsCount=2 Degree=2 IsPeriodic=0
    g226: GeomPoint X=322.073 Y=124.221 Z=0
    g227: GeomPoint X=318.073 Y=120.221 Z=0
    g228: Circle CenterX=322.073 CenterY=105.865 CenterZ=0 NormalX=0 NormalY=0 NormalZ=1 AngleXU=0 Radius=1
    g229: Circle CenterX=318.073 CenterY=105.865 CenterZ=0 NormalX=0 NormalY=0 NormalZ=1 AngleXU=0 Radius=1
    g230: Circle CenterX=318.073 CenterY=109.865 CenterZ=0 NormalX=0 NormalY=0 NormalZ=1 AngleXU=0 Radius=1
    g231: BSplineCurve PolesCount=3 KnotsCount=2 Degree=2 IsPeriodic=0
    g232: GeomPoint X=322.073 Y=105.865 Z=0
    g233: GeomPoint X=318.073 Y=109.865 Z=0
    g234: Circle CenterX=336.157 CenterY=107.779 CenterZ=0 NormalX=0 NormalY=0 NormalZ=1 AngleXU=0 Radius=1
    g235: Circle CenterX=332.651 CenterY=105.853 CenterZ=0 NormalX=0 NormalY=0 NormalZ=1 AngleXU=0 Radius=1
    g236: Circle CenterX=328.643 CenterY=105.865 CenterZ=0 NormalX=0 NormalY=0 NormalZ=1 AngleXU=0 Radius=1
    g237: BSplineCurve PolesCount=3 KnotsCount=2 Degree=2 IsPeriodic=0
    g238: GeomPoint X=336.157 Y=107.779 Z=0
    g239: GeomPoint X=328.643 Y=105.865 Z=0
    g240: LineSegment StartX=322.073 StartY=124.221 StartZ=0 EndX=362.073 EndY=124.221 EndZ=0
    g241: Circle CenterX=371.567 CenterY=-80.8644 CenterZ=0 NormalX=0 NormalY=0 NormalZ=1 AngleXU=0 Radius=1
    g242: Circle CenterX=375.073 CenterY=-82.7896 CenterZ=0 NormalX=0 NormalY=0 NormalZ=1 AngleXU=0 Radius=1
    g243: Circle CenterX=375.073 CenterY=-78.7896 CenterZ=0 NormalX=0 NormalY=0 NormalZ=1 AngleXU=0 Radius=1
    g244: BSplineCurve PolesCount=3 KnotsCount=2 Degree=2 IsPeriodic=0
    g245: GeomPoint X=371.567 Y=-80.8644 Z=0
    g246: GeomPoint X=375.073 Y=-78.7896 Z=0
    g247: Circle CenterX=321.579 CenterY=-53.4075 CenterZ=0 NormalX=0 NormalY=0 NormalZ=1 AngleXU=0 Radius=1
    g248: Circle CenterX=318.073 CenterY=-51.4823 CenterZ=0 NormalX=0 NormalY=0 NormalZ=1 AngleXU=0 Radius=1
    g249: Circle CenterX=318.073 CenterY=-47.4805 CenterZ=0 NormalX=0 NormalY=0 NormalZ=1 AngleXU=0 Radius=1
    g250: BSplineCurve PolesCount=3 KnotsCount=2 Degree=2 IsPeriodic=0
    g251: GeomPoint X=321.579 Y=-53.4075 Z=0
    g252: GeomPoint X=318.073 Y=-47.4805 Z=0
    g253: LineSegment StartX=371.567 StartY=-80.8644 StartZ=0 EndX=321.579 EndY=-53.4075 EndZ=0
    g254: Circle CenterX=321.579 CenterY=-67.3492 CenterZ=0 NormalX=0 NormalY=0 NormalZ=1 AngleXU=0 Radius=1
    g255: Circle CenterX=318.073 CenterY=-65.424 CenterZ=0 NormalX=0 NormalY=0 NormalZ=1 AngleXU=0 Radius=1
    g256: Circle CenterX=318.073 CenterY=-69.424 CenterZ=0 NormalX=0 NormalY=0 NormalZ=1 AngleXU=0 Radius=1
    g257: BSplineCurve PolesCount=3 KnotsCount=2 Degree=2 IsPeriodic=0
    g258: GeomPoint X=321.579 Y=-67.3492 Z=0
    g259: GeomPoint X=318.073 Y=-69.424 Z=0
    g260: Circle CenterX=362.567 CenterY=-89.8542 CenterZ=0 NormalX=0 NormalY=0 NormalZ=1 AngleXU=0 Radius=1
    g261: Circle CenterX=366.073 CenterY=-91.7794 CenterZ=0 NormalX=0 NormalY=0 NormalZ=1 AngleXU=0 Radius=1
    g262: Circle CenterX=362.073 CenterY=-91.7794 CenterZ=0 NormalX=0 NormalY=0 NormalZ=1 AngleXU=0 Radius=1
    g263: BSplineCurve PolesCount=3 KnotsCount=2 Degree=2 IsPeriodic=0
    g264: GeomPoint X=362.567 Y=-89.8542 Z=0
    g265: GeomPoint X=362.073 Y=-91.7794 Z=0
    g266: Circle CenterX=322.073 CenterY=-91.7794 CenterZ=0 NormalX=0 NormalY=0 NormalZ=1 AngleXU=0 Radius=1
    g267: Circle CenterX=318.073 CenterY=-91.7794 CenterZ=0 NormalX=0 NormalY=0 NormalZ=1 AngleXU=0 Radius=1
    g268: Circle CenterX=318.073 CenterY=-87.7794 CenterZ=0 NormalX=0 NormalY=0 NormalZ=1 AngleXU=0 Radius=1
    g269: BSplineCurve PolesCount=3 KnotsCount=2 Degree=2 IsPeriodic=0
    g270: GeomPoint X=322.073 Y=-91.7794 Z=0
    g271: GeomPoint X=318.073 Y=-87.7794 Z=0
    g272: LineSegment StartX=362.567 StartY=-89.8542 StartZ=0 EndX=321.579 EndY=-67.3492 EndZ=0
    g273: LineSegment StartX=318.073 StartY=-69.424 StartZ=0 EndX=318.073 EndY=-87.7794 EndZ=0
    g274: LineSegment StartX=322.073 StartY=-91.7794 StartZ=0 EndX=362.073 EndY=-91.7794 EndZ=0
    g275: Circle CenterX=2.07281 CenterY=124.221 CenterZ=0 NormalX=0 NormalY=0 NormalZ=1 AngleXU=0 Radius=1
    g276: Circle CenterX=1.57905 CenterY=122.295 CenterZ=0 NormalX=0 NormalY=0 NormalZ=1 AngleXU=0 Radius=1
    g277: BSplineCurve PolesCount=3 KnotsCount=2 Degree=2 IsPeriodic=0
    g278: GeomPoint X=2.07281 Y=124.221 Z=0
    g279: GeomPoint X=1.57905 Y=122.295 Z=0
    g280: Circle CenterX=42.0728 CenterY=124.221 CenterZ=0 NormalX=0 NormalY=0 NormalZ=1 AngleXU=0 Radius=1
    g281: Circle CenterX=46.0728 CenterY=124.221 CenterZ=0 NormalX=0 NormalY=0 NormalZ=1 AngleXU=0 Radius=1
    g282: Circle CenterX=46.0728 CenterY=120.221 CenterZ=0 NormalX=0 NormalY=0 NormalZ=1 AngleXU=0 Radius=1
    g283: BSplineCurve PolesCount=3 KnotsCount=2 Degree=2 IsPeriodic=0
    g284: GeomPoint X=42.0728 Y=124.221 Z=0
    g285: GeomPoint X=46.0728 Y=120.221 Z=0
    g286: Circle CenterX=46.0728 CenterY=109.865 CenterZ=0 NormalX=0 NormalY=0 NormalZ=1 AngleXU=0 Radius=1
    g287: Circle CenterX=46.0728 CenterY=105.865 CenterZ=0 NormalX=0 NormalY=0 NormalZ=1 AngleXU=0 Radius=1
    g288: Circle CenterX=42.0728 CenterY=105.865 CenterZ=0 NormalX=0 NormalY=0 NormalZ=1 AngleXU=0 Radius=1
    g289: BSplineCurve PolesCount=3 KnotsCount=2 Degree=2 IsPeriodic=0
    g290: GeomPoint X=46.0728 Y=109.865 Z=0
    g291: GeomPoint X=42.0728 Y=105.865 Z=0
    g292: Circle CenterX=35.5028 CenterY=105.865 CenterZ=0 NormalX=0 NormalY=0 NormalZ=1 AngleXU=0 Radius=1
    g293: Circle CenterX=31.5028 CenterY=105.865 CenterZ=0 NormalX=0 NormalY=0 NormalZ=1 AngleXU=0 Radius=1
    g294: Circle CenterX=27.9965 CenterY=107.79 CenterZ=0 NormalX=0 NormalY=0 NormalZ=1 AngleXU=0 Radius=1
    g295: BSplineCurve PolesCount=3 KnotsCount=2 Degree=2 IsPeriodic=0
    g296: GeomPoint X=35.5028 Y=105.865 Z=0
    g297: GeomPoint X=27.9965 Y=107.79 Z=0
    g298: LineSegment StartX=2.07281 StartY=124.221 StartZ=0 EndX=42.0728 EndY=124.221 EndZ=0
    g299: LineSegment StartX=46.0728 StartY=120.221 StartZ=0 EndX=46.0728 EndY=109.865 EndZ=0
    g300: LineSegment StartX=42.0728 StartY=105.865 StartZ=0 EndX=35.5028 EndY=105.865 EndZ=0
    g301: LineSegment StartX=27.9965 StartY=107.79 StartZ=0 EndX=1.57905 EndY=122.295 EndZ=0
    g302: Circle CenterX=42.5666 CenterY=-67.3492 CenterZ=0 NormalX=0 NormalY=0 NormalZ=1 AngleXU=0 Radius=1
    g303: Circle CenterX=46.0728 CenterY=-65.424 CenterZ=0 NormalX=0 NormalY=0 NormalZ=1 AngleXU=0 Radius=1
    g304: Circle CenterX=46.0728 CenterY=-69.424 CenterZ=0 NormalX=0 NormalY=0 NormalZ=1 AngleXU=0 Radius=1
    g305: BSplineCurve PolesCount=3 KnotsCount=2 Degree=2 IsPeriodic=0
    g306: GeomPoint X=42.5666 Y=-67.3492 Z=0
    g307: GeomPoint X=46.0728 Y=-69.424 Z=0
    g308: Circle CenterX=46.0728 CenterY=-87.7794 CenterZ=0 NormalX=0 NormalY=0 NormalZ=1 AngleXU=0 Radius=1
    g309: Circle CenterX=46.0728 CenterY=-91.7794 CenterZ=0 NormalX=0 NormalY=0 NormalZ=1 AngleXU=0 Radius=1
    g310: Circle CenterX=42.0728 CenterY=-91.7794 CenterZ=0 NormalX=0 NormalY=0 NormalZ=1 AngleXU=0 Radius=1
    g311: BSplineCurve PolesCount=3 KnotsCount=2 Degree=2 IsPeriodic=0
    g312: GeomPoint X=46.0728 Y=-87.7794 Z=0
    g313: GeomPoint X=42.0728 Y=-91.7794 Z=0
    g314: Circle CenterX=2.07281 CenterY=-91.7794 CenterZ=0 NormalX=0 NormalY=0 NormalZ=1 AngleXU=0 Radius=1
    g315: Circle CenterX=-1.92719 CenterY=-91.7794 CenterZ=0 NormalX=0 NormalY=0 NormalZ=1 AngleXU=0 Radius=1
    g316: Circle CenterX=1.57905 CenterY=-89.8542 CenterZ=0 NormalX=0 NormalY=0 NormalZ=1 AngleXU=0 Radius=1
    g317: BSplineCurve PolesCount=3 KnotsCount=2 Degree=2 IsPeriodic=0
    g318: GeomPoint X=2.07281 Y=-91.7794 Z=0
    g319: GeomPoint X=1.57905 Y=-89.8542 Z=0
    g320: LineSegment StartX=2.07281 StartY=-91.7794 StartZ=0 EndX=42.0728 EndY=-91.7794 EndZ=0
    g321: LineSegment StartX=46.0728 StartY=-87.7794 StartZ=0 EndX=46.0728 EndY=-69.424 EndZ=0
    g322: LineSegment StartX=42.5666 StartY=-67.3492 StartZ=0 EndX=1.57905 EndY=-89.8542 EndZ=0
    g323: Circle CenterX=322.073 CenterY=76.4095 CenterZ=0 NormalX=0 NormalY=0 NormalZ=1 AngleXU=0 Radius=4
    g324: BSplineCurve PolesCount=3 KnotsCount=2 Degree=2 IsPeriodic=0
    g325: GeomPoint X=318.073 Y=72.4095 Z=0
    g326: GeomPoint X=322.073 Y=76.4095 Z=0
    g327: Circle CenterX=375.073 CenterY=72.4095 CenterZ=0 NormalX=0 NormalY=0 NormalZ=1 AngleXU=0 Radius=1
    g328: Circle CenterX=375.073 CenterY=76.4095 CenterZ=0 NormalX=0 NormalY=0 NormalZ=1 AngleXU=0 Radius=1
    g329: Circle CenterX=371.073 CenterY=76.4095 CenterZ=0 NormalX=0 NormalY=0 NormalZ=1 AngleXU=0 Radius=1
    g330: BSplineCurve PolesCount=3 KnotsCount=2 Degree=2 IsPeriodic=0
    g331: GeomPoint X=375.073 Y=72.4095 Z=0
    g332: GeomPoint X=371.073 Y=76.4095 Z=0
    g333: LineSegment StartX=322.073 StartY=76.4095 StartZ=0 EndX=371.073 EndY=76.4095 EndZ=0
    g334: LineSegment StartX=318.073 StartY=72.4095 StartZ=0 EndX=318.073 EndY=-47.4805 EndZ=0
    g335: LineSegment StartX=375.073 StartY=72.4095 StartZ=0 EndX=375.073 EndY=-78.7896 EndZ=0
    g336: ArcOfCircle CenterX=-26.9272 CenterY=22.1087 CenterZ=0 NormalX=0 NormalY=0 NormalZ=1 AngleXU=0 Radius=4 StartAngle=5e-16 EndAngle=3.14159
    g337: LineSegment StartX=-22.9272 StartY=22.1087 StartZ=0 EndX=-18.9272 EndY=-83.7794 EndZ=0
    g338: LineSegment StartX=-34.9272 StartY=-83.7794 StartZ=0 EndX=-30.9272 EndY=22.1087 EndZ=0
    g339: ArcOfCircle CenterX=391.073 CenterY=22.1087 CenterZ=0 NormalX=0 NormalY=0 NormalZ=1 AngleXU=0 Radius=4 StartAngle=0 EndAngle=3.14159
    g340: LineSegment StartX=387.073 StartY=22.1087 StartZ=0 EndX=383.073 EndY=-83.7794 EndZ=0
    g341: LineSegment StartX=395.073 StartY=22.1087 StartZ=0 EndX=399.073 EndY=-83.7794 EndZ=0
    g342: Circle CenterX=-10.9272 CenterY=-78.7794 CenterZ=0 NormalX=0 NormalY=0 NormalZ=1 AngleXU=0 Radius=1
    g343: Circle CenterX=-10.9272 CenterY=-82.7794 CenterZ=0 NormalX=0 NormalY=0 NormalZ=1 AngleXU=0 Radius=1
    g344: Circle CenterX=-7.42095 CenterY=-80.8542 CenterZ=0 NormalX=0 NormalY=0 NormalZ=1 AngleXU=0 Radius=1
    g345: BSplineCurve PolesCount=3 KnotsCount=2 Degree=2 IsPeriodic=0
    g346: GeomPoint X=-10.9272 Y=-78.7794 Z=0
    g347: GeomPoint X=-7.42095 Y=-80.8542 Z=0
    g348: Circle CenterX=42.5666 CenterY=-53.4075 CenterZ=0 NormalX=0 NormalY=0 NormalZ=1 AngleXU=0 Radius=1
    g349: Circle CenterX=46.0728 CenterY=-51.4823 CenterZ=0 NormalX=0 NormalY=0 NormalZ=1 AngleXU=0 Radius=1
    g350: Circle CenterX=46.0728 CenterY=-47.4823 CenterZ=0 NormalX=0 NormalY=0 NormalZ=1 AngleXU=0 Radius=1
    g351: BSplineCurve PolesCount=3 KnotsCount=2 Degree=2 IsPeriodic=0
    g352: GeomPoint X=42.5666 Y=-53.4075 Z=0
    g353: GeomPoint X=46.0728 Y=-47.4823 Z=0
    g354: Circle CenterX=46.0728 CenterY=72.4095 CenterZ=0 NormalX=0 NormalY=0 NormalZ=1 AngleXU=0 Radius=1
    g355: Circle CenterX=46.0728 CenterY=76.4095 CenterZ=0 NormalX=0 NormalY=0 NormalZ=1 AngleXU=0 Radius=1
    g356: Circle CenterX=42.0728 CenterY=76.4095 CenterZ=0 NormalX=0 NormalY=0 NormalZ=1 AngleXU=0 Radius=1
    g357: BSplineCurve PolesCount=3 KnotsCount=2 Degree=2 IsPeriodic=0
    g358: GeomPoint X=46.0728 Y=72.4095 Z=0
    g359: GeomPoint X=42.0728 Y=76.4095 Z=0
    g360: Circle CenterX=-6.92718 CenterY=76.4095 CenterZ=0 NormalX=0 NormalY=0 NormalZ=1 AngleXU=0 Radius=1
    g361: Circle CenterX=-10.9272 CenterY=76.4095 CenterZ=0 NormalX=0 NormalY=0 NormalZ=1 AngleXU=0 Radius=1
    g362: Circle CenterX=-10.9272 CenterY=72.4095 CenterZ=0 NormalX=0 NormalY=0 NormalZ=1 AngleXU=0 Radius=1
    g363: BSplineCurve PolesCount=3 KnotsCount=2 Degree=2 IsPeriodic=0
    g364: GeomPoint X=-6.92718 Y=76.4095 Z=0
    g365: GeomPoint X=-10.9272 Y=72.4095 Z=0
    g366: LineSegment StartX=-10.9272 StartY=72.4095 StartZ=0 EndX=-10.9272 EndY=-78.7794 EndZ=0
    g367: LineSegment StartX=-7.42095 StartY=-80.8542 StartZ=0 EndX=42.5666 EndY=-53.4075 EndZ=0
    g368: LineSegment StartX=46.0728 StartY=-47.4823 StartZ=0 EndX=46.0728 EndY=72.4095 EndZ=0
    g369: LineSegment StartX=42.0728 StartY=76.4095 StartZ=0 EndX=-6.92719 EndY=76.4095 EndZ=0
    g370: LineSegment StartX=232.072 StartY=136.221 StartZ=0 EndX=232.072 EndY=-117.815 EndZ=0
    g371: LineSegment StartX=132.072 StartY=136.221 StartZ=0 EndX=132.072 EndY=-121.309 EndZ=0
    g372: LineSegment StartX=245.072 StartY=136.221 StartZ=0 EndX=245.072 EndY=-116.499 EndZ=0
    g373: LineSegment StartX=119.072 StartY=136.221 StartZ=0 EndX=119.072 EndY=-116.228 EndZ=0
    g374: LineSegment StartX=-42.9272 StartY=136.221 StartZ=0 EndX=407.073 EndY=136.221 EndZ=0
    g375: LineSegment StartX=232.072 StartY=136.221 StartZ=0 EndX=220.072 EndY=136.221 EndZ=0
    g376: LineSegment StartX=232.072 StartY=136.221 StartZ=0 EndX=232.072 EndY=124.221 EndZ=0
    g377: LineSegment StartX=220.072 StartY=136.221 StartZ=0 EndX=220.072 EndY=124.221 EndZ=0
    g378: LineSegment StartX=220.072 StartY=136.221 StartZ=0 EndX=226.072 EndY=136.221 EndZ=0
    g379: LineSegment StartX=220.072 StartY=136.221 StartZ=0 EndX=220.072 EndY=130.221 EndZ=0
    g380: LineSegment StartX=220.072 StartY=124.221 StartZ=0 EndX=226.072 EndY=124.221 EndZ=0
    g381: LineSegment StartX=232.072 StartY=124.221 StartZ=0 EndX=232.072 EndY=127.221 EndZ=0
    g382: LineSegment StartX=232.072 StartY=136.221 StartZ=0 EndX=232.072 EndY=133.221 EndZ=0
    g383-g387: Circle x5 (B-spline internal-alignment scaffolding for g388; pole/knot coordinates omitted)
    g388: BSplineCurve PolesCount=5 KnotsCount=3 Degree=3 IsPeriodic=0
    g389: GeomPoint X=232.072 Y=133.221 Z=0
    g390: GeomPoint X=223.072 Y=130.221 Z=0
    g391: GeomPoint X=232.072 Y=127.221 Z=0
    g392: LineSegment StartX=189.124 StartY=124.221 StartZ=0 EndX=302.073 EndY=124.221 EndZ=0
    g393: LineSegment StartX=132.072 StartY=136.221 StartZ=0 EndX=132.072 EndY=124.221 EndZ=0
    g394: LineSegment StartX=132.072 StartY=136.221 StartZ=0 EndX=144.072 EndY=136.221 EndZ=0
    g395: LineSegment StartX=144.072 StartY=136.221 StartZ=0 EndX=144.072 EndY=124.221 EndZ=0
    g396: LineSegment StartX=144.072 StartY=124.221 StartZ=0 EndX=138.072 EndY=124.221 EndZ=0
    g397: LineSegment StartX=144.072 StartY=136.221 StartZ=0 EndX=138.072 EndY=136.221 EndZ=0
    g398: LineSegment StartX=144.072 StartY=136.221 StartZ=0 EndX=144.072 EndY=130.221 EndZ=0
    g399: LineSegment StartX=132.072 StartY=136.221 StartZ=0 EndX=132.072 EndY=133.221 EndZ=0
    g400: LineSegment StartX=132.072 StartY=133.221 StartZ=0 EndX=132.072 EndY=127.221 EndZ=0
  constraints (682):
    c: Vertical(g0)
    c: Vertical(g1)
    c: Block(g1)
    c: Block(g0)
    c: Weight(g4) = 1
    c: Equal(g4,g5)
    c: Equal(g4,g6)
    c: InternalAlignment(g4,g7)
    c: InternalAlignment(g5,g7)
    c: InternalAlignment(g6,g7)
    c: InternalAlignment(g8,g7)
    c: InternalAlignment(g9,g7)
    c: Weight(g10) = 1
    c: Equal(g10,g11)
    c: Equal(g10,g12)
    c: InternalAlignment(g10,g13)
    c: InternalAlignment(g11,g13)
    c: InternalAlignment(g12,g13)
    c: InternalAlignment(g14,g13)
    c: InternalAlignment(g15,g13)
    c: Block(g13)
    c: Block(g7)
    c: Weight(g16) = 1
    c: Equal(g16,g17)
    c: Equal(g16,g18)
    c: InternalAlignment(g16,g19)
    c: InternalAlignment(g17,g19)
    c: InternalAlignment(g18,g19)
    c: InternalAlignment(g20,g19)
    c: InternalAlignment(g21,g19)
    c: Weight(g22) = 1
    c: Equal(g22,g23)
    c: Equal(g22,g24)
    c: InternalAlignment(g22,g25)
    c: InternalAlignment(g23,g25)
    c: InternalAlignment(g24,g25)
    c: InternalAlignment(g26,g25)
    c: InternalAlignment(g27,g25)
    c: Block(g25)
    c: Block(g19)
    c: Weight(g28) = 1
    c: Equal(g28,g29)
    c: Equal(g28,g30)
    c: InternalAlignment(g28,g31)
    c: InternalAlignment(g29,g31)
    c: InternalAlignment(g30,g31)
    c: InternalAlignment(g32,g31)
    c: InternalAlignment(g33,g31)
    c: Weight(g34) = 1
    c: Equal(g34,g35)
    c: Equal(g34,g36)
    c: InternalAlignment(g34,g37)
    c: InternalAlignment(g35,g37)
    c: InternalAlignment(g36,g37)
    c: InternalAlignment(g38,g37)
    c: InternalAlignment(g39,g37)
    c: Block(g31)
    c: Block(g37)
    c: Coincident(g40,g1)
    c: Coincident(g40,g0)
    c: Horizontal(g40)
    c: Distance(g40) = 450
    c: Weight(g41) = 1
    c: Equal(g41,g42)
    c: Equal(g41,g43)
    c: InternalAlignment(g41,g44)
    c: InternalAlignment(g42,g44)
    c: InternalAlignment(g43,g44)
    c: InternalAlignment(g45,g44)
    c: InternalAlignment(g46,g44)
    c: Block(g44)
    c: Weight(g47) = 1
    c: Equal(g47,g48)
    c: Equal(g47,g49)
    c: InternalAlignment(g47,g50)
    c: InternalAlignment(g48,g50)
    c: InternalAlignment(g49,g50)
    c: InternalAlignment(g51,g50)
    c: InternalAlignment(g52,g50)
    c: Block(g50)
    c: Weight(g53) = 1
    c: Equal(g53,g54)
    c: Equal(g53,g55)
    c: InternalAlignment(g53,g56)
    c: InternalAlignment(g54,g56)
    c: InternalAlignment(g55,g56)
    c: InternalAlignment(g57,g56)
    c: InternalAlignment(g58,g56)
    c: Block(g56)
    c: Weight(g59) = 1
    c: Equal(g59,g60)
    c: Equal(g59,g61)
    c: InternalAlignment(g59,g62)
    c: InternalAlignment(g60,g62)
    c: InternalAlignment(g61,g62)
    c: InternalAlignment(g63,g62)
    c: InternalAlignment(g64,g62)
    c: Block(g62)
    c: Weight(g65) = 1
    c: Equal(g65,g66)
    c: Equal(g65,g67)
    c: InternalAlignment(g65,g68)
    c: InternalAlignment(g66,g68)
    c: InternalAlignment(g67,g68)
    c: InternalAlignment(g69,g68)
    c: InternalAlignment(g70,g68)
    c: Weight(g71) = 1
    c: Equal(g71,g72)
    c: Equal(g71,g73)
    c: InternalAlignment(g71,g74)
    c: InternalAlignment(g72,g74)
    c: InternalAlignment(g73,g74)
    c: InternalAlignment(g75,g74)
    c: InternalAlignment(g76,g74)
    c: Block(g68)
    c: Block(g74)
    c: Coincident(g77,g68)
    c: Coincident(g77,g74)
    c: Vertical(g77)
    c: Coincident(g78,g68)
    c: Coincident(g78,g50)
    c: Coincident(g79,g50)
    c: Coincident(g79,g74)
    c: Weight(g80) = 1
    c: Equal(g80,g81)
    c: Equal(g80,g82)
    c: InternalAlignment(g80,g83)
    c: InternalAlignment(g81,g83)
    c: InternalAlignment(g82,g83)
    c: InternalAlignment(g84,g83)
    c: InternalAlignment(g85,g83)
    c: Weight(g86) = 1
    c: Equal(g86,g87)
    c: Equal(g86,g88)
    c: InternalAlignment(g86,g89)
    c: InternalAlignment(g87,g89)
    c: InternalAlignment(g88,g89)
    c: InternalAlignment(g90,g89)
    c: InternalAlignment(g91,g89)
    c: Block(g83)
    c: Block(g89)
    c: Coincident(g92,g83)
    c: Coincident(g92,g89)
    c: Vertical(g92)
    c: Coincident(g93,g83)
    c: Coincident(g93,g44)
    c: Coincident(g94,g44)
    c: Coincident(g94,g89)
    c: Weight(g95) = 1
    c: Equal(g95,g96)
    c: Equal(g95,g97)
    c: InternalAlignment(g95,g98)
    c: InternalAlignment(g96,g98)
    c: InternalAlignment(g97,g98)
    c: InternalAlignment(g99,g98)
    c: InternalAlignment(g100,g98)
    c: Weight(g101) = 1
    c: Equal(g101,g102)
    c: Equal(g101,g103)
    c: InternalAlignment(g101,g104)
    c: InternalAlignment(g102,g104)
    c: InternalAlignment(g103,g104)
    c: InternalAlignment(g105,g104)
    c: InternalAlignment(g106,g104)
    c: Block(g98)
    c: Block(g104)
    c: Coincident(g107,g98)
    c: Coincident(g107,g104)
    c: Vertical(g107)
    c: Coincident(g108,g104)
    c: Coincident(g108,g62)
    c: Coincident(g109,g62)
    c: Coincident(g109,g98)
    c: Weight(g110) = 1
    c: Equal(g110,g111)
    c: Equal(g110,g112)
    c: InternalAlignment(g110,g113)
    c: InternalAlignment(g111,g113)
    c: InternalAlignment(g112,g113)
    c: InternalAlignment(g114,g113)
    c: InternalAlignment(g115,g113)
    c: Weight(g116) = 1
    c: Equal(g116,g117)
    c: Equal(g116,g118)
    c: InternalAlignment(g116,g119)
    c: InternalAlignment(g117,g119)
    c: InternalAlignment(g118,g119)
    c: InternalAlignment(g120,g119)
    c: InternalAlignment(g121,g119)
    c: Block(g113)
    c: Block(g119)
    c: Coincident(g122,g113)
    c: Coincident(g122,g119)
    c: Vertical(g122)
    c: Coincident(g123,g119)
    c: Coincident(g123,g56)
    c: Coincident(g124,g56)
    c: Coincident(g124,g113)
    c: Weight(g125) = 1
    c: Equal(g125,g126)
    c: Equal(g125,g127)
    c: InternalAlignment(g125,g128)
    c: InternalAlignment(g126,g128)
    c: InternalAlignment(g127,g128)
    c: InternalAlignment(g129,g128)
    c: InternalAlignment(g130,g128)
    c: Weight(g131) = 1
    c: Equal(g131,g132)
    c: Equal(g131,g133)
    c: InternalAlignment(g131,g134)
    c: InternalAlignment(g132,g134)
    c: InternalAlignment(g133,g134)
    c: InternalAlignment(g135,g134)
    c: InternalAlignment(g136,g134)
    c: Weight(g137) = 1
    c: Equal(g137,g138)
    c: Equal(g137,g139)
    c: InternalAlignment(g137,g140)
    c: InternalAlignment(g138,g140)
    c: InternalAlignment(g139,g140)
    c: InternalAlignment(g141,g140)
    c: InternalAlignment(g142,g140)
    c: Weight(g143) = 1
    c: Equal(g143,g144)
    c: Equal(g143,g145)
    c: InternalAlignment(g143,g146)
    c: InternalAlignment(g144,g146)
    c: InternalAlignment(g145,g146)
    c: InternalAlignment(g147,g146)
    c: InternalAlignment(g148,g146)
    c: Block(g146)
    c: Block(g140)
    c: Block(g134)
    c: Block(g128)
    c: Coincident(g149,g25)
    c: Coincident(g149,g146)
    c: Coincident(g150,g146)
    c: Coincident(g150,g140)
    c: Horizontal(g150)
    c: Coincident(g151,g140)
    c: Coincident(g151,g25)
    c: Vertical(g151)
    c: Coincident(g152,g19)
    c: Coincident(g152,g134)
    c: Vertical(g152)
    c: Coincident(g153,g134)
    c: Coincident(g153,g128)
    c: Horizontal(g153)
    c: Coincident(g154,g128)
    c: Coincident(g154,g19)
    c: Weight(g155) = 1
    c: Equal(g155,g156)
    c: Equal(g155,g157)
    c: InternalAlignment(g155,g158)
    c: InternalAlignment(g156,g158)
    c: InternalAlignment(g157,g158)
    c: InternalAlignment(g159,g158)
    c: InternalAlignment(g160,g158)
    c: Weight(g161) = 1
    c: Equal(g161,g162)
    c: Equal(g161,g163)
    c: InternalAlignment(g161,g164)
    c: InternalAlignment(g162,g164)
    c: InternalAlignment(g163,g164)
    c: InternalAlignment(g165,g164)
    c: InternalAlignment(g166,g164)
    c: Weight(g167) = 1
    c: Equal(g167,g168)
    c: Equal(g167,g169)
    c: InternalAlignment(g167,g170)
    c: InternalAlignment(g168,g170)
    c: InternalAlignment(g169,g170)
    c: InternalAlignment(g171,g170)
    c: InternalAlignment(g172,g170)
    c: Weight(g173) = 1
    c: Equal(g173,g174)
    c: Equal(g173,g175)
    c: InternalAlignment(g173,g176)
    c: InternalAlignment(g174,g176)
    c: InternalAlignment(g175,g176)
    c: InternalAlignment(g177,g176)
    c: InternalAlignment(g178,g176)
    c: Block(g176)
    c: Block(g170)
    c: Block(g164)
    c: Block(g158)
    c: Coincident(g179,g170)
    c: Coincident(g179,g7)
    c: Vertical(g179)
    c: Coincident(g180,g13)
    c: Coincident(g180,g164)
    c: Vertical(g180)
    c: Coincident(g181,g158)
    c: Coincident(g181,g13)
    c: Coincident(g182,g7)
    c: Weight(g183) = 1
    c: Equal(g183,g184)
    c: Equal(g183,g185)
    c: InternalAlignment(g183,g186)
    c: InternalAlignment(g184,g186)
    c: InternalAlignment(g185,g186)
    c: InternalAlignment(g187,g186)
    c: InternalAlignment(g188,g186)
    c: Weight(g189) = 1
    c: Equal(g189,g190)
    c: Equal(g189,g191)
    c: InternalAlignment(g189,g192)
    c: InternalAlignment(g190,g192)
    c: InternalAlignment(g191,g192)
    c: InternalAlignment(g193,g192)
    c: InternalAlignment(g194,g192)
    c: Block(g192)
    c: Block(g186)
    c: Coincident(g195,g192)
    c: Coincident(g195,g31)
    c: Coincident(g196,g31)
    c: Coincident(g196,g186)
    c: Coincident(g197,g186)
    c: Coincident(g197,g192)
    c: Vertical(g197)
    c: Weight(g198) = 1
    c: Equal(g198,g199)
    c: Equal(g198,g200)
    c: InternalAlignment(g198,g201)
    c: InternalAlignment(g199,g201)
    c: InternalAlignment(g200,g201)
    c: InternalAlignment(g202,g201)
    c: InternalAlignment(g203,g201)
    c: Weight(g204) = 1
    c: Equal(g204,g205)
    c: Equal(g204,g206)
    c: InternalAlignment(g204,g207)
    c: InternalAlignment(g205,g207)
    c: InternalAlignment(g206,g207)
    c: InternalAlignment(g208,g207)
    c: InternalAlignment(g209,g207)
    c: Block(g207)
    c: Block(g201)
    c: Coincident(g210,g201)
    c: Coincident(g210,g37)
    c: Coincident(g211,g37)
    c: Coincident(g211,g207)
    c: Coincident(g212,g207)
    c: Coincident(g212,g201)
    c: Vertical(g212)
    c: Horizontal(g213)
    c: Block(g213)
    c: Vertical(g214)
    c: Block(g214)
    c: Block(g215)
    c: Weight(g216) = 1
    c: Equal(g216,g217)
    c: Equal(g216,g218)
    c: InternalAlignment(g216,g219)
    c: InternalAlignment(g217,g219)
    c: InternalAlignment(g218,g219)
    c: InternalAlignment(g220,g219)
    c: InternalAlignment(g221,g219)
    c: Weight(g222) = 1
    c: Equal(g222,g223)
    c: Equal(g222,g224)
    c: InternalAlignment(g222,g225)
    c: InternalAlignment(g223,g225)
    c: InternalAlignment(g224,g225)
    c: InternalAlignment(g226,g225)
    c: InternalAlignment(g227,g225)
    c: Weight(g228) = 1
    c: Equal(g228,g229)
    c: Equal(g228,g230)
    c: InternalAlignment(g228,g231)
    c: InternalAlignment(g229,g231)
    c: InternalAlignment(g230,g231)
    c: InternalAlignment(g232,g231)
    c: InternalAlignment(g233,g231)
    c: Weight(g234) = 1
    c: Equal(g234,g235)
    c: Equal(g234,g236)
    c: InternalAlignment(g234,g237)
    c: InternalAlignment(g235,g237)
    c: InternalAlignment(g236,g237)
    c: InternalAlignment(g238,g237)
    c: InternalAlignment(g239,g237)
    c: Block(g219)
    c: Block(g225)
    c: Block(g231)
    c: Block(g237)
    c: Coincident(g240,g225)
    c: Coincident(g240,g219)
    c: Horizontal(g240)
    c: Block(g182)
    c: Weight(g241) = 1
    c: Equal(g241,g242)
    c: Equal(g241,g243)
    c: InternalAlignment(g241,g244)
    c: InternalAlignment(g242,g244)
    c: InternalAlignment(g243,g244)
    c: InternalAlignment(g245,g244)
    c: InternalAlignment(g246,g244)
    c: Weight(g247) = 1
    c: Equal(g247,g248)
    c: Equal(g247,g249)
    c: InternalAlignment(g247,g250)
    c: InternalAlignment(g248,g250)
    c: InternalAlignment(g249,g250)
    c: InternalAlignment(g251,g250)
    c: InternalAlignment(g252,g250)
    c: Block(g244)
    c: Block(g250)
    c: Coincident(g253,g244)
    c: Coincident(g253,g250)
    c: Weight(g254) = 1
    c: Equal(g254,g255)
    c: Equal(g254,g256)
    c: InternalAlignment(g254,g257)
    c: InternalAlignment(g255,g257)
    c: InternalAlignment(g256,g257)
    c: InternalAlignment(g258,g257)
    c: InternalAlignment(g259,g257)
    c: Weight(g260) = 1
    c: Equal(g260,g261)
    c: Equal(g260,g262)
    c: InternalAlignment(g260,g263)
    c: InternalAlignment(g261,g263)
    c: InternalAlignment(g262,g263)
    c: InternalAlignment(g264,g263)
    c: InternalAlignment(g265,g263)
    c: Weight(g266) = 1
    c: Equal(g266,g267)
    c: Equal(g266,g268)
    c: InternalAlignment(g266,g269)
    c: InternalAlignment(g267,g269)
    c: InternalAlignment(g268,g269)
    c: InternalAlignment(g270,g269)
    c: InternalAlignment(g271,g269)
    c: Block(g269)
    c: Block(g263)
    c: Block(g257)
    c: Coincident(g272,g263)
    c: Coincident(g272,g257)
    c: Coincident(g273,g257)
    c: Coincident(g273,g269)
    c: Vertical(g273)
    c: Coincident(g274,g269)
    c: Coincident(g274,g263)
    c: Horizontal(g274)
    c: Weight(g275) = 1
    c: Equal(g275,g276)
    c: InternalAlignment(g275,g277)
    c: InternalAlignment(g276,g277)
    c: InternalAlignment(g278,g277)
    c: InternalAlignment(g279,g277)
    c: Weight(g280) = 1
    c: InternalAlignment(g281,g283)
    c: InternalAlignment(g282,g283)
    c: InternalAlignment(g284,g283)
    c: InternalAlignment(g285,g283)
    c: Weight(g286) = 1
    c: Equal(g286,g287)
    c: Equal(g286,g288)
    c: InternalAlignment(g286,g289)
    c: InternalAlignment(g287,g289)
    c: InternalAlignment(g288,g289)
    c: InternalAlignment(g290,g289)
    c: InternalAlignment(g291,g289)
    c: Equal(g292,g293)
    c: Equal(g292,g294)
    c: InternalAlignment(g292,g295)
    c: InternalAlignment(g293,g295)
    c: InternalAlignment(g294,g295)
    c: InternalAlignment(g296,g295)
    c: InternalAlignment(g297,g295)
    c: Block(g283)
    c: Block(g289)
    c: Block(g295)
    c: Block(g277)
    c: Coincident(g298,g277)
    c: Coincident(g298,g283)
    c: Horizontal(g298)
    c: Coincident(g299,g283)
    c: Coincident(g299,g289)
    c: Vertical(g299)
    c: Coincident(g300,g289)
    c: Coincident(g300,g295)
    c: Horizontal(g300)
    c: Coincident(g301,g295)
    c: Coincident(g301,g277)
    c: Weight(g302) = 1
    c: Equal(g302,g303)
    c: Equal(g302,g304)
    c: InternalAlignment(g302,g305)
    c: InternalAlignment(g303,g305)
    c: InternalAlignment(g304,g305)
    c: InternalAlignment(g306,g305)
    c: InternalAlignment(g307,g305)
    c: Weight(g308) = 1
    c: Equal(g308,g309)
    c: Equal(g308,g310)
    c: InternalAlignment(g308,g311)
    c: InternalAlignment(g309,g311)
    c: InternalAlignment(g310,g311)
    c: InternalAlignment(g312,g311)
    c: Weight(g314) = 1
    c: Equal(g314,g315)
    c: Equal(g314,g316)
    c: InternalAlignment(g314,g317)
    c: InternalAlignment(g315,g317)
    c: InternalAlignment(g316,g317)
    c: InternalAlignment(g318,g317)
    c: InternalAlignment(g319,g317)
    c: Block(g317)
    c: Block(g311)
    c: Block(g305)
    c: Coincident(g320,g317)
    c: Coincident(g320,g311)
    c: Horizontal(g320)
    c: Coincident(g321,g311)
    c: Coincident(g321,g305)
    c: Vertical(g321)
    c: Coincident(g322,g305)
    c: Coincident(g322,g317)
    c: InternalAlignment(g323,g324)
    c: InternalAlignment(g325,g324)
    c: InternalAlignment(g326,g324)
    c: Block(g324)
    c: Equal(g327,g328)
    c: Equal(g327,g329)
    c: InternalAlignment(g327,g330)
    c: InternalAlignment(g328,g330)
    c: InternalAlignment(g329,g330)
    c: InternalAlignment(g331,g330)
    c: InternalAlignment(g332,g330)
    c: Block(g330)
    c: Coincident(g333,g324)
    c: Horizontal(g333)
    c: Block(g333)
    c: Coincident(g334,g324)
    c: Coincident(g334,g250)
    c: Vertical(g334)
    c: Coincident(g335,g330)
    c: Coincident(g335,g244)
    c: Vertical(g335)
    c: Block(g336)
    c: Block(g2)
    c: Distance(g334) = 119.89
    c: Coincident(g337,g336)
    c: Coincident(g337,g2)
    c: Coincident(g338,g2)
    c: Coincident(g338,g336)
    c: Block(g3)
    c: Block(g339)
    c: Coincident(g340,g339)
    c: Coincident(g340,g3)
    c: Coincident(g341,g339)
    c: Coincident(g341,g3)
    c: Block(g341)
    c: Block(g340)
    c: Weight(g342) = 1
    c: Equal(g342,g343)
    c: Equal(g342,g344)
    c: InternalAlignment(g342,g345)
    c: InternalAlignment(g343,g345)
    c: InternalAlignment(g344,g345)
    c: InternalAlignment(g346,g345)
    c: InternalAlignment(g347,g345)
    c: Weight(g348) = 1
    c: Equal(g348,g349)
    c: Equal(g348,g350)
    c: InternalAlignment(g348,g351)
    c: InternalAlignment(g349,g351)
    c: InternalAlignment(g350,g351)
    c: InternalAlignment(g352,g351)
    c: InternalAlignment(g353,g351)
    c: Weight(g354) = 1
    c: Equal(g354,g355)
    c: Equal(g354,g356)
    c: InternalAlignment(g354,g357)
    c: InternalAlignment(g355,g357)
    c: InternalAlignment(g356,g357)
    c: InternalAlignment(g358,g357)
    c: InternalAlignment(g359,g357)
    c: Weight(g360) = 1
    c: Equal(g360,g361)
    c: Equal(g360,g362)
    c: InternalAlignment(g360,g363)
    c: InternalAlignment(g361,g363)
    c: InternalAlignment(g362,g363)
    c: InternalAlignment(g364,g363)
    c: InternalAlignment(g365,g363)
    c: Block(g363)
    c: Block(g357)
    c: Block(g351)
    c: Block(g345)
    c: Coincident(g366,g363)
    c: Coincident(g366,g345)
    c: Vertical(g366)
    c: Coincident(g367,g345)
    c: Coincident(g367,g351)
    c: Coincident(g368,g351)
    c: Coincident(g368,g357)
    c: Vertical(g368)
    c: Coincident(g369,g357)
    c: Coincident(g369,g363)
    c: Horizontal(g369)
    c: Vertical(g370)
    c: Vertical(g371)
    c: Vertical(g372)
    c: Vertical(g373)
    c: Coincident(g374,g0)
    c: Coincident(g374,g1)
    c: Horizontal(g374)
    c: Block(g374)
    c: Distance(g374) = 450
    c: Block(g372)
    c: Block(g370)
    c: Block(g371)
    c: Block(g373)
    c: Distance(g0) = 240
    c: Horizontal(g375)
    c: Distance(g375) = 12
    c: Coincident(g375,g370)
    c: Vertical(g376)
    c: Distance(g376) = 12
    c: Coincident(g376,g370)
    c: Coincident(g377,g375)
    c: Vertical(g377)
    c: Horizontal(g378)
    c: Vertical(g379)
    c: Distance(g379) = 6
    c: Coincident(g379,g375)
    c: Coincident(g378,g375)
    c: Block(g377)
    c: Coincident(g380,g377)
    c: Horizontal(g380)
    c: Distance(g380) = 6
    c: Vertical(g381)
    c: Distance(g381) = 3
    c: Vertical(g382)
    c: Distance(g382) = 3
    c: Coincident(g382,g370)
    c: Coincident(g376,g381)
    c: Coincident(g388,g382)
    c: Weight(g383) = 1
    c: Equal(g383,g384)
    c: Coincident(g384,g378)
    c: Equal(g383,g385)
    c: Coincident(g385,g379)
    c: Equal(g383,g386)
    c: Coincident(g386,g380)
    c: Equal(g383,g387)
    c: Coincident(g388,g381)
    c: InternalAlignment(g383-g387 -> g388) x5
    c: InternalAlignment(g389,g388)
    c: InternalAlignment(g390,g388)
    c: InternalAlignment(g391,g388)
    c: Coincident(g392,g164)
    c: Coincident(g392,g158)
    c: Horizontal(g392)
    c: Block(g388)
    c: Vertical(g393)
    c: Distance(g393) = 12
    c: Coincident(g393,g371)
    c: Horizontal(g394)
    c: Distance(g394) = 12
    c: Coincident(g394,g371)
    c: Coincident(g395,g394)
    c: Vertical(g395)
    c: Distance(g395) = 12
    c: Coincident(g396,g395)
    c: Horizontal(g396)
    c: Distance(g396) = 6
    c: Horizontal(g397)
    c: Distance(g397) = 6
    c: Coincident(g397,g394)
    c: Vertical(g398)
    c: Distance(g398) = 6
    c: Coincident(g398,g394)
    c: Vertical(g399)
    c: Distance(g399) = 3
    c: Coincident(g399,g371)
    c: Vertical(g400)
    c: Distance(g400) = 6
    c: Coincident(g400,g399)
FEATURE [Part::Extrusion] Extrude005
  Base = -> Sketch003
  Dir = (0,0,1)
  DirMode = 2
  FaceMakerClass = Part::FaceMakerBullseye
  LengthFwd = 24
  LengthRev = 0
  Solid = true
  Symmetric = false
